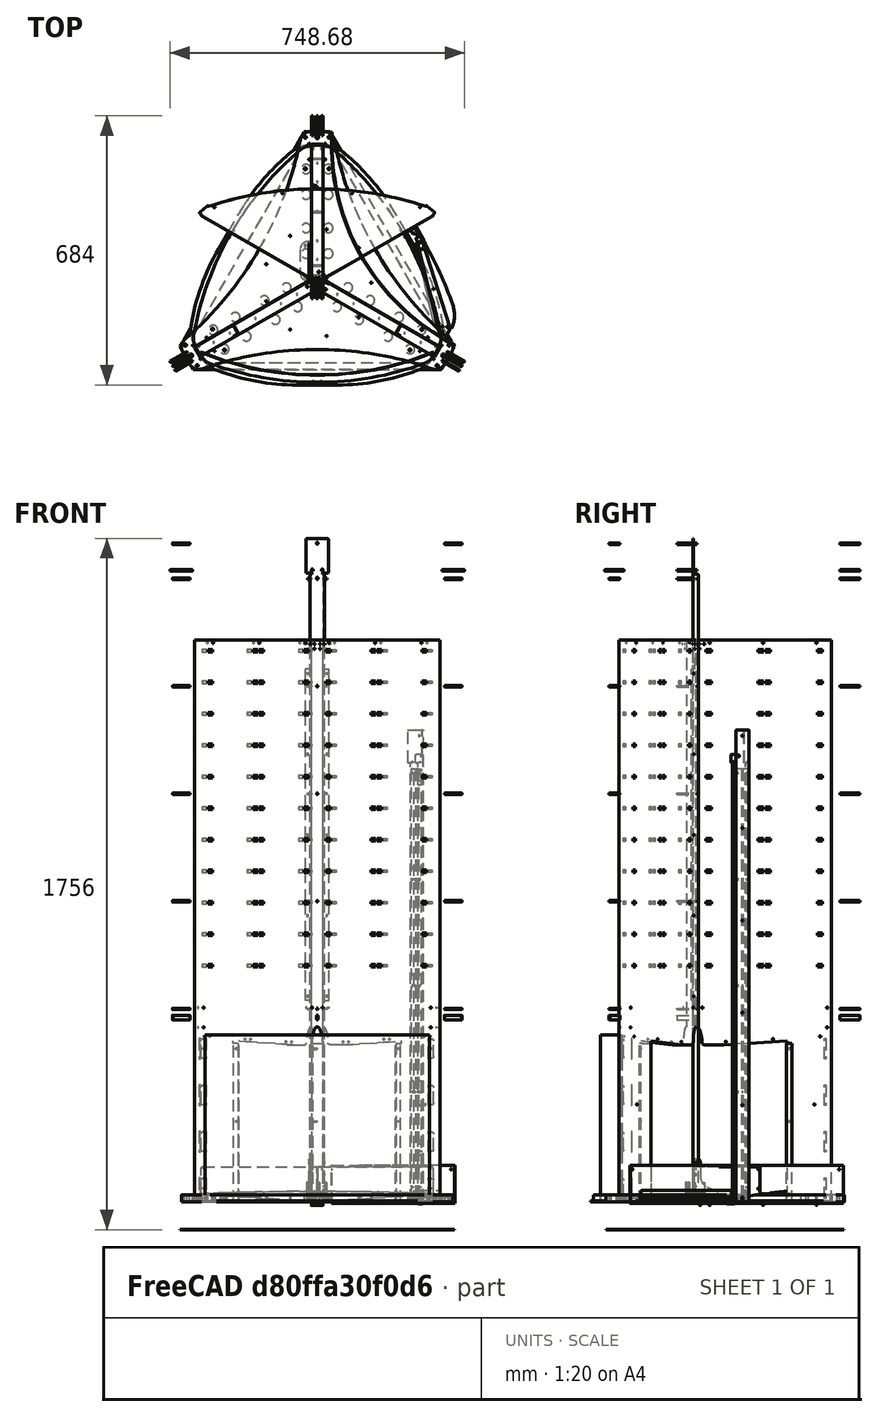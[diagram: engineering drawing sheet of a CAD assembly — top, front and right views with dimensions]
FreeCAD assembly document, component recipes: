
FREECAD ASSEMBLY — COMPONENT RECIPES ("composit_full_size3_door")

This assembly document has 79 components, labeled P0..P78 below (a component is one placed body or linked part). 75 of them carry a construction recipe — the FreeCAD feature program that regenerates the part from scratch, quoted from this document or its linked companion documents; the rest are supplied as boundary geometry only. No exploded tour is included for this assembly.
NOTE — document 3 of 3 of this assembly tour. The two overview renders and the header above are repeated from document 1; the component sections below continue where the previous document stopped.
COMPONENT P63 — recipe-attached ("sink_material_0.30ansi001", modeled in this document).
Construction recipe (the document's own serialized feature program — sketch geometry with constraints, then the solid features built on it; lengths are millimeters unless a unit is written):

FEATURE [Sketcher::SketchObject] Sketch037
  AttachmentSupport = -> [XY_Plane028]
  FullyConstrained = false
  MapMode = 5
  sketch-geometry (2):
    g0: LineSegment StartX=0 StartY=0 StartZ=0 EndX=74.4649 EndY=59.2839 EndZ=0
    g1: LineSegment StartX=0 StartY=0 StartZ=0 EndX=-93.8109 EndY=73.3435 EndZ=0
  constraints (2):
    c: Coincident(g0,g-1)
    c: Coincident(g1,g0)
FEATURE [Part::Part2DObjectPython] Line  label="sink_bend_line"  # Draft 2D object (typed FeaturePython)
  Area = 0
  AttachmentOffset = pos=(304.73,175.936,20) rot=(0,0,1;0rad)
  AttachmentSupport = -> [XY_Plane028]
  BendAngle = 6.48542
  ChamferSize = 0
  Closed = false
  End = (0,0,0)
  FaceAngle = 3.2479
  FilletRadius = 0
  Length = 352.44
  MakeFace = true
  MapMode = 5
  Placement = pos=(304.73,175.936,20) rot=(0,0,1;0rad)
  Points = (2) [(0,0,0),(-304.73,-175.936,-20)]
  Start = (304.73,175.936,20)
  Subdivisions = 0
  expr: .AttachmentOffset.Base.x = Spreadsheet.total_length * cos(30)
  expr: .AttachmentOffset.Base.y = Spreadsheet.total_length * sin(30)
  expr: BendAngle = atan2(.AttachmentOffset.Base.z; .AttachmentOffset.Base.y)
  expr: End = tuple(0; 0; 0)
  expr: FaceAngle = atan2(.AttachmentOffset.Base.z; Length)
FEATURE [PartDesign::Line] DatumLine
  AttacherType = Attacher::AttachEngineLine
  AttachmentSupport = -> [Z_Axis028]
  Length = 20
  MapMode = 29
  ResizeMode = 0
FEATURE [PartDesign::Line] DatumLine001
  AttacherType = Attacher::AttachEngineLine
  AttachmentSupport = -> [Line,X_Axis028]
  Length = 20
  MapMode = 24
  Placement = pos=(304.73,175.936,20) rot=(0.57735,-0.57735,-0.57735;2.0944rad)
  ResizeMode = 0
FEATURE [Sketcher::SketchObject] Sketch038
  AttachmentSupport = -> [Line]
  ExternalGeometry = -> [DatumLine001]
  FullyConstrained = false
  MapMode = 45
  Placement = pos=(152.365,87.9679,10) rot=(0.368581,0.6384,0.675717;2.39766rad)
  sketch-geometry (3):
    g0: LineSegment StartX=4.75e-14 StartY=4.27e-14 StartZ=0 EndX=4.75e-14 EndY=93.8582 EndZ=0
    g1: LineSegment StartX=4.75e-14 StartY=4.27e-14 StartZ=0 EndX=35.2298 EndY=3.46271 EndZ=0
    g2: ArcOfCircle CenterX=2.5 CenterY=2.75777 CenterZ=0 NormalX=0 NormalY=0 NormalZ=1 AngleXU=0 Radius=2.5 StartAngle=3.14159 EndAngle=4.81036
  constraints (9):
    c: Coincident(g0,g-1)
    c: Vertical(g0)
    c: Coincident(g1,g0)
    c: PointOnObject(g1,g-3)
    c: Angle(g-3) = 0.0979746
    c: Angle(g1,g0) = 1.47282  'bend_angle'
    c: Tangent(g2,g0) = 1.5708
    c: Tangent(g2,g1) = -1.5708
    c: Radius(g2) = 2.5
FEATURE [PartDesign::CoordinateSystem] Local_CS
  AttacherType = Attacher::AttachEngine3D
  AttachmentOffset = pos=(0,0,0) rot=(1,0,0;0.113192rad)
  AttachmentSupport = -> [XY_Plane028]
  MapMode = 5
  Placement = pos=(0,0,0) rot=(1,0,0;0.113192rad)
  expr: .AttachmentOffset.Rotation.Angle = Line.BendAngle
FEATURE [Sketcher::SketchObject] Sketch039
  AttachmentSupport = -> [Local_CS]
  ExternalGeometry = -> [Line,Sketch038]
  FullyConstrained = true
  MapMode = 5
  Placement = pos=(0,0,0) rot=(1,0,0;0.113192rad)
  sketch-geometry (3):
    g0: LineSegment StartX=2e-16 StartY=3.18954 StartZ=0 EndX=-459.172 EndY=270 EndZ=0
    g1: LineSegment StartX=2e-16 StartY=3.18954 StartZ=0 EndX=459.172 EndY=270 EndZ=0
    g2: LineSegment StartX=459.172 StartY=270 StartZ=0 EndX=-459.172 EndY=270 EndZ=0
  constraints (8):
    c: Coincident(g2,g1)
    c: DistanceY(g1) = 270
    c: Coincident(g0,g2)
    c: Symmetric(g1,g0,g-2)
    c: Coincident(g1,g0)
    c: PointOnObject(g0,g-2)
    c: Parallel(g1,g-3)
    c: PointOnObject(g-4,g1)
FEATURE [PartDesign::FeaturePython] BaseBend011  # WARN: FeaturePython — macro-defined, semantics opaque (R4)
  BendSide = 0
  BendSketch = -> Sketch039
  MidPlane = false
  Reverse = false
  Suppressed = false
  length = 100
  radius = 2
  thickness = 0.5
FEATURE [PartDesign::FeaturePython] Bend004  # WARN: FeaturePython — macro-defined, semantics opaque (R4)
  AutoMiter = false
  BaseFeature = -> BaseBend011
  BendType = 0
  LengthList = [100]
  LengthSpec = 1
  ReliefFactor = 0.7
  Suppressed = false
  UseReliefFactor = false
  angle = 95.6135
  baseObject = -> BaseBend011 [Edge3,Edge8]
  bendAList = [95.6135]
  extend1 = 2
  extend2 = 0
  gap1 = 0
  gap2 = 0
  invert = true
  kfactor = 0.5
  length = 100
  maxExtendDist = 5
  minGap = 0.1
  minReliefGap = 1
  miterangle1 = 0
  miterangle2 = 0
  offset = 0
  radius = 2
  reliefType = 0
  reliefd = 1
  reliefw = 0.8
  sketchflip = false
  sketchinvert = false
  unfold = false
  expr: angle = 180 deg - Sketch038.Constraints.bend_angle
  expr: radius = BaseBend011.radius
FEATURE [Sketcher::SketchObject] Sketch040
  AttachmentSupport = -> [Local_CS]
  ExternalGeometry = -> [Line,Sketch038]
  FullyConstrained = true
  MapMode = 5
  Placement = pos=(0,0,0) rot=(1,0,0;0.113192rad)
  sketch-geometry (13):
    g0: ArcOfCircle CenterX=0 CenterY=-630 CenterZ=0 NormalX=0 NormalY=0 NormalZ=1 AngleXU=0 Radius=870 StartAngle=1.24863 EndAngle=1.89296
    g1: LineSegment StartX=0 StartY=0 StartZ=0 EndX=294.959 EndY=171.391 EndZ=0
    g2: LineSegment StartX=150.979 StartY=90.9189 StartZ=0 EndX=293.573 EndY=173.776 EndZ=0
    g3: LineSegment StartX=-294.959 StartY=171.391 StartZ=0 EndX=0 EndY=0 EndZ=0
    g4: LineSegment StartX=-294.959 StartY=171.391 StartZ=0 EndX=-464.661 EndY=270 EndZ=0
    g5: LineSegment StartX=-464.661 StartY=270 StartZ=0 EndX=464.661 EndY=270 EndZ=0
    g6: LineSegment StartX=464.661 StartY=270 StartZ=0 EndX=294.959 EndY=171.391 EndZ=0
    g7: LineSegment StartX=294.959 StartY=171.391 StartZ=0 EndX=294.075 EndY=172.911 EndZ=0
    g8: LineSegment StartX=294.075 StartY=172.911 StartZ=0 EndX=293.573 EndY=173.776 EndZ=0
    g9: LineSegment StartX=-294.959 StartY=171.391 StartZ=0 EndX=-294.959 EndY=171.391 EndZ=0
    g10: LineSegment StartX=293.573 StartY=173.776 StartZ=0 EndX=275.46 EndY=195.241 EndZ=0
    g11: LineSegment StartX=-293.573 StartY=173.776 StartZ=0 EndX=-275.46 EndY=195.241 EndZ=0
    g12: LineSegment StartX=-294.959 StartY=171.391 StartZ=0 EndX=-293.573 EndY=173.776 EndZ=0
  constraints (34):
    c: Coincident(g1,g-1)
    c: PointOnObject(g1,g-3)
    c: Coincident(g7,g1)
    c: Distance(g1) = 341.139
    c: Coincident(g2,g-4)
    c: Parallel(g2,g1)
    c: DistanceY(g0) = -630
    c: Radius(g0) = 870
    c: Coincident(g9,g3)
    c: Coincident(g3,g1)
    c: Symmetric(g9,g7,g-2)
    c: Coincident(g4,g5)
    c: Coincident(g5,g6)
    c: Parallel(g6,g2)
    c: Symmetric(g5,g4,g-2)
    c: DistanceY(g5) = 270
    c: Coincident(g2,g8)
    c: Coincident(g7,g8)
    c: Perpendicular(g1,g7)
    c: Perpendicular(g1,g8)
    c: Distance(g8) = 1
    c: Coincident(g10,g0)
    c: Coincident(g11,g0)
    c: PointOnObject(g0,g-2)
    c: Coincident(g10,g8)
    c: Coincident(g12,g9)
    c: Coincident(g4,g12)
    c: Coincident(g12,g11)
    c: Symmetric(g4,g6,g-2)
    c: Symmetric(g8,g11,g-2)
    c: Horizontal(g0,g0)
    c: Distance(g10) = 28.0862
    c: Angle(g10,g2) = 1.39626
    c: Coincident(g6,g7)
FEATURE [PartDesign::SubShapeBinder] Binder031
  BindCopyOnChange = 0
  BindMode = 0
  ClaimChildren = false
  Context = -> Part007 [Body020.Binder031.]
  Fuse = false
  MakeFace = true
  OffsetFill = false
  OffsetIntersection = false
  OffsetJoinType = 0
  OffsetOpenResult = false
  PartialLoad = false
  Relative = true
  _Version = 2
FEATURE [PartDesign::Pocket] Pocket022
  BaseFeature = -> Bend004
  Direction = (0,0.11295,-0.993601)
  Length = 2.5
  Length2 = 5
  Profile = -> Sketch040
  ReferenceAxis = -> Sketch040 [N_Axis]
  Refine = true
  Reversed = true
  Suppressed = false
  Type = 0
FEATURE [Sketcher::SketchObject] Sketch042
  AttachmentSupport = -> [XY_Plane028]
  FullyConstrained = true
  MapMode = 5
  sketch-geometry (7):
    g0: LineSegment StartX=-18.3205 StartY=-10 StartZ=0 EndX=-0.5 EndY=0.288675 EndZ=0
    g1: LineSegment StartX=18.3205 StartY=-10 StartZ=0 EndX=-18.3205 EndY=-10 EndZ=0
    g2: LineSegment StartX=1 StartY=1.5e-15 StartZ=0 EndX=-1e-16 EndY=0.57735 EndZ=0
    g3: LineSegment StartX=1.3e-15 StartY=-2.2e-15 StartZ=0 EndX=0.5 EndY=0.288675 EndZ=0
    g4: LineSegment StartX=0.5 StartY=0.288675 StartZ=0 EndX=18.3205 EndY=-10 EndZ=0
    g5: LineSegment StartX=-2.6e-15 StartY=1.1547 StartZ=0 EndX=0.5 EndY=0.288675 EndZ=0
    g6: LineSegment StartX=-0.5 StartY=0.288675 StartZ=0 EndX=-2.6e-15 EndY=1.1547 EndZ=0
  constraints (19):
    c: Coincident(g4,g1)
    c: Coincident(g1,g0)
    c: Symmetric(g4,g0,g-2)
    c: PointOnObject(g2,g-1)
    c: PointOnObject(g2,g-2)
    c: Angle(g2) = 2.61799
    c: Distance(g-1,g2) = 0.5
    c: Coincident(g3,g-1)
    c: PointOnObject(g3,g2)
    c: Angle(g3) = 0.523599
    c: PointOnObject(g2,g4)
    c: Perpendicular(g3,g5)
    c: Coincident(g4,g5)
    c: Coincident(g4,g3)
    c: PointOnObject(g5,g-2)
    c: Coincident(g6,g0)
    c: Coincident(g6,g5)
    c: Symmetric(g4,g0,g-2)
    c: DistanceY(g1) = -10
FEATURE [Sketcher::SketchObject] Sketch041
  AttachmentOffset = pos=(0,0,0) rot=(0,1,0;0.523599rad)
  AttachmentSupport = -> [XZ_Plane028]
  ExternalGeometry = -> [Sketch038,Sketch042,Sketch040]
  FullyConstrained = false
  MapMode = 5
  Placement = pos=(0,0,0) rot=(0.935113,0.250563,0.250563;1.63783rad)
  sketch-geometry (16):
    g0: LineSegment StartX=340.573 StartY=19.628 StartZ=0 EndX=340.432 EndY=22.112 EndZ=0
    g1: LineSegment StartX=175.779 StartY=12.7533 StartZ=0 EndX=340.432 EndY=22.112 EndZ=0
    g2: LineSegment StartX=0.57735 StartY=196.491 StartZ=0 EndX=638.392 EndY=196.491 EndZ=0
    g3: LineSegment StartX=638.392 StartY=196.491 StartZ=0 EndX=638.392 EndY=36.5557 EndZ=0
    g4: LineSegment StartX=638.392 StartY=36.5557 StartZ=0 EndX=340.573 EndY=19.628 EndZ=0
    g5: LineSegment StartX=340.432 StartY=22.112 StartZ=0 EndX=340.432 EndY=85 EndZ=0
    g6: LineSegment StartX=0.57735 StartY=85 StartZ=0 EndX=0.57735 EndY=196.491 EndZ=0
    g7: LineSegment StartX=335.432 StartY=90 StartZ=0 EndX=5.57735 EndY=90 EndZ=0
    g8: ArcOfCircle CenterX=5.57735 CenterY=85 CenterZ=0 NormalX=0 NormalY=0 NormalZ=1 AngleXU=0 Radius=5 StartAngle=1.5708 EndAngle=3.14159
    g9: ArcOfCircle CenterX=335.432 CenterY=85 CenterZ=0 NormalX=0 NormalY=0 NormalZ=1 AngleXU=0 Radius=5 StartAngle=2e-16 EndAngle=1.5708
    g10: GeomPoint X=340.432 Y=90 Z=0
    g11: LineSegment StartX=0.57735 StartY=0 StartZ=0 EndX=0.57735 EndY=27.6603 EndZ=0
    g12: ArcOfCircle CenterX=5 CenterY=27.6603 CenterZ=0 NormalX=0 NormalY=0 NormalZ=1 AngleXU=0 Radius=4.42265 StartAngle=3.14159 EndAngle=4.18879
    g13: ArcOfCircle CenterX=0.57735 CenterY=20 CenterZ=0 NormalX=0 NormalY=0 NormalZ=1 AngleXU=0 Radius=4.42265 StartAngle=-2.31e-14 EndAngle=1.0472
    g14: LineSegment StartX=5 StartY=20 StartZ=0 EndX=5 EndY=0 EndZ=0
    g15: LineSegment StartX=5 StartY=0 StartZ=0 EndX=0.57735 EndY=0 EndZ=0
  constraints (39):
    c: Coincident(g1,g-3)
    c: Coincident(g1,g0)
    c: Perpendicular(g-3,g1)
    c: Perpendicular(g1,g0)
    c: Coincident(g5,g0)
    c: Coincident(g6,g2)
    c: Horizontal(g2)
    c: Coincident(g2,g3)
    c: Vertical(g3)
    c: Coincident(g3,g4)
    c: Coincident(g4,g0)
    c: Parallel(g4,g1)
    c: Vertical(g5)
    c: Vertical(g6)
    c: Vertical(g6,g-4)
    c: Horizontal(g7)
    c: Tangent(g8,g7) = -1.5708
    c: Tangent(g8,g6) = 1.5708
    c: PointOnObject(g10,g5)
    c: PointOnObject(g10,g7)
    c: Tangent(g5,g9) = -1.5708
    c: Tangent(g7,g9) = -1.5708
    c: Equal(g9,g8)
    c: Coincident(g11,g-4)
    c: Vertical(g11)
    c: PointOnObject(g13,g11)
    c: PointOnObject(g14,g-1)
    c: Vertical(g14)
    c: Coincident(g15,g14)
    c: Coincident(g15,g11)
    c: Tangent(g13,g12) = 1.5708
    c: Tangent(g12,g11) = 1.5708
    c: Tangent(g14,g13) = 1.5708
    c: Equal(g13,g12)
    c: DistanceX(g14) = 5
    c: DistanceY(g13) = 20
    c: DistanceY(g7) = 90
    c: Radius(g9) = 5
    c: Coincident(g0,g-5)
FEATURE [Sketcher::SketchObject] Sketch043
  AttachmentSupport = -> [Local_CS]
  FullyConstrained = false
  MapMode = 5
  Placement = pos=(0,0,0) rot=(1,0,0;0.113192rad)
  expr: Constraints[12] = Sketch038.Constraints.bend_angle / 2
  sketch-geometry (7):
    g0: ArcOfCircle CenterX=-2.2e-14 CenterY=1.72e-14 CenterZ=0 NormalX=0 NormalY=0 NormalZ=1 AngleXU=0 Radius=19.4106 StartAngle=5.52221 EndAngle=10.1858
    g1: ArcOfCircle CenterX=17.4885 CenterY=-16.6545 CenterZ=0 NormalX=0 NormalY=0 NormalZ=1 AngleXU=0 Radius=4.73935 StartAngle=2.38062 EndAngle=3.72466
    g2: ArcOfCircle CenterX=-17.4885 CenterY=-16.6545 CenterZ=0 NormalX=0 NormalY=0 NormalZ=1 AngleXU=0 Radius=4.73935 StartAngle=5.70012 EndAngle=7.04416
    g3: LineSegment StartX=13.5322 StartY=-19.2639 StartZ=0 EndX=49.1398 EndY=-73.2508 EndZ=0
    g4: LineSegment StartX=-13.5322 StartY=-19.2639 StartZ=0 EndX=-49.1398 EndY=-73.2508 EndZ=0
    g5: LineSegment StartX=-49.1398 StartY=-73.2508 StartZ=0 EndX=49.1398 EndY=-73.2508 EndZ=0
    g6: LineSegment StartX=-86.3387 StartY=-141.994 StartZ=0 EndX=130.665 EndY=54.7259 EndZ=0
  constraints (13):
    c: Coincident(g0,g-1)
    c: Coincident(g5,g4)
    c: Coincident(g5,g3)
    c: Tangent(g3,g1) = -1.5708
    c: Tangent(g1,g0) = 1.5708
    c: Tangent(g2,g0) = 1.5708
    c: Tangent(g4,g2) = 1.5708
    c: Symmetric(g4,g3,g-2)
    c: Symmetric(g2,g1,g-2)
    c: DistanceX(g1) = 13.5322
    c: DistanceY(g1) = -19.2639
    c: Angle(g3) = -0.987729
    c: Angle(g6) = 0.736411
FEATURE [Sketcher::SketchObject] Sketch064
  AttachmentSupport = -> [Local_CS]
  FullyConstrained = true
  MapMode = 5
  Placement = pos=(0,0,0) rot=(1,0,0;0.113192rad)
  expr: Constraints[3] = <<Properties>>.rivet_d
  sketch-geometry (4):
    g0: Circle CenterX=-88.3 CenterY=228.865 CenterZ=0 NormalX=0 NormalY=0 NormalZ=1 AngleXU=0 Radius=1.7
    g1: Circle CenterX=88.3 CenterY=228.865 CenterZ=0 NormalX=0 NormalY=0 NormalZ=1 AngleXU=0 Radius=1.7
    g2: Circle CenterX=261.291 CenterY=193.3 CenterZ=0 NormalX=0 NormalY=0 NormalZ=1 AngleXU=0 Radius=1.7
    g3: Circle CenterX=-261.291 CenterY=193.3 CenterZ=0 NormalX=0 NormalY=0 NormalZ=1 AngleXU=0 Radius=1.7
  constraints (10):
    c: Equal(g2,g1)
    c: Equal(g2,g0)
    c: Equal(g2,g3)
    c: Diameter(g2) = 3.4
    c: DistanceX(g1) = 88.3
    c: DistanceY(g1) = 228.865
    c: DistanceX(g2) = 261.291
    c: DistanceY(g2) = 193.3
    c: Symmetric(g0,g1,g-2)
    c: Symmetric(g3,g2,g-2)
FEATURE [PartDesign::FeaturePython] Bend030  # WARN: FeaturePython — macro-defined, semantics opaque (R4)
  AutoMiter = true
  BaseFeature = -> Pocket022
  BendType = 0
  LengthList = [10]
  LengthSpec = 0
  ReliefFactor = 0.7
  Suppressed = false
  UseReliefFactor = false
  angle = 90
  baseObject = -> Pocket022 [Edge44,Edge42]
  bendAList = [90]
  extend1 = 0
  extend2 = 0
  gap1 = 0
  gap2 = 0
  invert = false
  kfactor = 0.5
  length = 10
  maxExtendDist = 5
  minGap = 0.1
  minReliefGap = 1
  miterangle1 = 0
  miterangle2 = 0
  offset = 0
  radius = 2
  reliefType = 0
  reliefd = 1
  reliefw = 0.8
  sketchflip = false
  sketchinvert = false
  unfold = true
  expr: radius = BaseBend011.radius
FEATURE [Sketcher::SketchObject] Sketch219
  AttachmentSupport = -> [Bend030]
  ExternalGeometry = -> [Bend030]
  FullyConstrained = true
  MapMode = 5
  Placement = pos=(0,-1.69e-14,1.483e-13) rot=(1,0,0;3.25479rad)
  sketch-geometry (6):
    g0: LineSegment StartX=297.803 StartY=-177.345 StartZ=0 EndX=303.917 EndY=-182.504 EndZ=0
    g1: LineSegment StartX=303.917 StartY=-182.504 StartZ=0 EndX=285.803 EndY=-203.969 EndZ=0
    g2: LineSegment StartX=285.803 StartY=-203.969 StartZ=0 EndX=276.608 EndY=-196.209 EndZ=0
    g3: LineSegment StartX=279.192 StartY=-196.205 StartZ=0 EndX=297.807 EndY=-180.398 EndZ=0
    g4: ArcOfCircle CenterX=296.513 CenterY=-178.873 CenterZ=0 NormalX=0 NormalY=0 NormalZ=1 AngleXU=0 Radius=2 StartAngle=5.41641 EndAngle=7.15307
    g5: ArcOfCircle CenterX=277.898 CenterY=-194.681 CenterZ=0 NormalX=0 NormalY=0 NormalZ=1 AngleXU=0 Radius=2 StartAngle=4.01147 EndAngle=5.41641
  constraints (15):
    c: Coincident(g0,g-3)
    c: Coincident(g0,g1)
    c: Coincident(g1,g-3)
    c: Coincident(g1,g2)
    c: Perpendicular(g1,g2)
    c: Perpendicular(g0,g1)
    c: Tangent(g4,g0) = 1.5708
    c: Tangent(g5,g2) = 1.5708
    c: Tangent(g5,g3) = -1.5708
    c: Tangent(g4,g3) = -1.5708
    c: Equal(g4,g5)
    c: Radius(g4) = 2
    c: Distance(g0) = 8
    c: Distance(g2) = 12.0319
    c: Distance(g3,g1) = 10.0593
FEATURE [PartDesign::Pocket] Pocket131
  BaseFeature = -> Bend030
  Direction = (0,-0.11295,0.993601)
  Length = 5
  Length2 = 5
  Profile = -> Sketch219
  ReferenceAxis = -> Sketch219 [N_Axis]
  Suppressed = false
  Type = 0
FEATURE [PartDesign::Mirrored] Mirrored017
  BaseFeature = -> Pocket131
  MirrorPlane = -> YZ_Plane028
  Originals = -> [Pocket131]
  Suppressed = false
FEATURE [PartDesign::Pocket] Pocket024
  BaseFeature = -> Mirrored017
  Direction = (0,0,-1)
  Length = 5
  Length2 = 5
  Midplane = true
  Profile = -> Sketch042
  ReferenceAxis = -> Sketch042 [N_Axis]
  Suppressed = false
  Type = 1
FEATURE [PartDesign::FeaturePython] CornerRelief  # WARN: FeaturePython — macro-defined, semantics opaque (R4)
  BaseFeature = -> Pocket024
  ReliefSketch = 0
  Size = 6
  SizeRatio = 1.5
  Sketch = -> Sketch043
  Suppressed = false
  XOffset = 0
  YOffset = 0
  baseObject = -> Pocket024 [Edge28,Edge31]
  kfactor = 0.5
FEATURE [PartDesign::Pocket] Pocket023
  BaseFeature = -> CornerRelief
  Direction = (-0.5,0.866025,-1e-16)
  Length = 0.6
  Length2 = 5
  Profile = -> Sketch041
  ReferenceAxis = -> Sketch041 [N_Axis]
  Suppressed = false
  Type = 0
FEATURE [PartDesign::Mirrored] Mirrored002
  BaseFeature = -> Pocket023
  MirrorPlane = -> YZ_Plane028
  Originals = -> [Pocket023]
  Refine = true
  Suppressed = false
FEATURE [PartDesign::Boolean] Boolean008
  BaseFeature = -> Mirrored002
  Group = -> [Compound028]
  Suppressed = false
  Type = 1
  UsePlacement = false
  expr: Group = <<sink_fix001>>._self
FEATURE [PartDesign::Pocket] Pocket029
  BaseFeature = -> Boolean008
  Direction = (0,0.11295,-0.993601)
  Length = 5
  Length2 = 5
  Profile = -> Sketch064
  ReferenceAxis = -> Sketch064 [N_Axis]
  Reversed = true
  Suppressed = false
  Type = 1
FEATURE [PartDesign::Body] Body020  label="sink_material_0.30ansi"
  Group = -> [Sketch037,Line,DatumLine,Sketch038,DatumLine001,Sketch039,BaseBend011,Bend004,Local_CS,Sketch040,Binder031,Pocket022,Sketch041,Sketch042,Bend030,Sketch219,Pocket131,Mirrored017,Pocket024,Sketch043,CornerRelief,Pocket023,Mirrored002,Boolean008,Sketch064,Pocket029]
  Origin = -> Origin028
  Tip = -> Pocket029
COMPONENT P64 — recipe-attached ("Body110", modeled in this document).
Construction recipe (the document's own serialized feature program — sketch geometry with constraints, then the solid features built on it; lengths are millimeters unless a unit is written):

FEATURE [PartDesign::SubShapeBinder] Binder061
  BindCopyOnChange = 0
  BindMode = 0
  ClaimChildren = false
  Context = -> Part007 [Body021.Binder061.]
  Fuse = false
  MakeFace = true
  OffsetFill = false
  OffsetIntersection = false
  OffsetJoinType = 0
  OffsetOpenResult = false
  PartialLoad = false
  Relative = false
  Support = -> [Body020[Pocket022.Sketch040.]]
  _Version = 2
FEATURE [PartDesign::SubShapeBinder] Binder062
  BindCopyOnChange = 0
  BindMode = 0
  ClaimChildren = false
  Context = -> Part007 [Body021.Binder062.]
  Fuse = false
  MakeFace = true
  OffsetFill = false
  OffsetIntersection = false
  OffsetJoinType = 0
  OffsetOpenResult = false
  PartialLoad = false
  Relative = false
  Support = -> [Body020[Pocket029.Sketch064.]]
  _Version = 2
FEATURE [Sketcher::SketchObject] Sketch109
  AttachmentSupport = -> [XY_Plane029]
  ExternalGeometry = -> [Binder061]
  FullyConstrained = false
  MapMode = 5
  sketch-geometry (19):
    g0: ArcOfCircle CenterX=291.996 CenterY=172.865 CenterZ=0 NormalX=0 NormalY=0 NormalZ=1 AngleXU=0 Radius=1 StartAngle=5.23599 EndAngle=6.98132
    g1: LineSegment StartX=5.51e-14 StartY=239 StartZ=0 EndX=5.51e-14 EndY=240 EndZ=0
    g2: LineSegment StartX=292.496 StartY=171.999 StartZ=0 EndX=287.719 EndY=169.241 EndZ=0
    g3: ArcOfCircle CenterX=287.219 CenterY=170.107 CenterZ=0 NormalX=0 NormalY=0 NormalZ=1 AngleXU=0 Radius=1 StartAngle=3.90153 EndAngle=5.23599
    g4: LineSegment StartX=5.51e-14 StartY=239 StartZ=0 EndX=5.51e-14 EndY=224 EndZ=0
    g5: ArcOfCircle CenterX=243.002 CenterY=128.086 CenterZ=0 NormalX=0 NormalY=0 NormalZ=1 AngleXU=0 Radius=60 StartAngle=0.759936 EndAngle=1.27733
    g6: GeomPoint X=287.033 Y=168.845 Z=0
    g7: GeomPoint X=293.528 Y=172.595 Z=0
    g8: ArcOfCircle CenterX=1.26657 CenterY=-621.999 CenterZ=0 NormalX=0 NormalY=0 NormalZ=1 AngleXU=0 Radius=862 StartAngle=1.25533 EndAngle=1.57227
    g9: LineSegment StartX=5.28e-14 StartY=220.8 StartZ=0 EndX=5.51e-14 EndY=240 EndZ=0
    g10: ArcOfCircle CenterX=0 CenterY=-641.2 CenterZ=0 NormalX=0 NormalY=0 NormalZ=1 AngleXU=0 Radius=862 StartAngle=1.25386 EndAngle=1.5708
    g11: LineSegment StartX=5.51e-14 StartY=240 StartZ=0 EndX=268.713 EndY=197.462 EndZ=0
    g12: LineSegment StartX=5.28e-14 StartY=220.8 StartZ=0 EndX=268.65 EndY=177.867 EndZ=0
    g13: ArcOfCircle CenterX=0 CenterY=-676.059 CenterZ=0 NormalX=0 NormalY=0 NormalZ=1 AngleXU=0 Radius=900.059 StartAngle=1.27733 EndAngle=1.5708
    g14: Circle CenterX=268.65 CenterY=177.867 CenterZ=0 NormalX=0 NormalY=0 NormalZ=1 AngleXU=0 Radius=4
    g15: LineSegment StartX=0 StartY=0 StartZ=0 EndX=301.632 EndY=174.148 EndZ=0
    g16: LineSegment StartX=0 StartY=0 StartZ=0 EndX=-15 EndY=25.9808 EndZ=0
    g17: ArcOfCircle CenterX=262.507 CenterY=178.449 CenterZ=0 NormalX=0 NormalY=0 NormalZ=1 AngleXU=0 Radius=20 StartAngle=0.698132 EndAngle=1.25533
    g18: LineSegment StartX=292.762 StartY=173.508 StartZ=0 EndX=277.828 EndY=191.305 EndZ=0
  constraints (51):
    c: Tangent(g17,g8) = -1.5708
    c: Vertical(g1)
    c: PointOnObject(g1,g-2)
    c: Angle(g2) = -2.61799
    c: Tangent(g2,g0) = 1.5708
    c: DistanceY(g1,g1) = 1
    c: Tangent(g3,g2) = 1.5708
    c: Radius(g3) = 1
    c: Equal(g3,g0)
    c: Coincident(g4,g1)
    c: Vertical(g4)
    c: Distance(g4) = 15
    c: Tangent(g5,g3) = 1.5708
    c: PointOnObject(g7,g2)
    c: PointOnObject(g6,g2)
    c: PointOnObject(g6,g5)
    c: Coincident(g8,g1)
    c: PointOnObject(g9,g-2)
    c: DistanceY(g9,g4) = 3.2
    c: Coincident(g9,g1)
    c: Radius(g8) = 862  'outer_r'
    c: Distance(g6,g7) = 7.5
    c: PointOnObject(g10,g-2)
    c: Coincident(g11,g1)
    c: Coincident(g11,g17)
    c: Coincident(g12,g10)
    c: Coincident(g12,g10)
    c: Equal(g10,g8)
    c: Equal(g12,g11)
    c: Coincident(g10,g9)
    c: PointOnObject(g13,g-2)
    c: Coincident(g13,g4)
    c: Tangent(g13,g5) = -1.5708
    c: Coincident(g14,g10)
    c: Tangent(g14,g5)
    c: Radius(g14) = 4
    c: Coincident(g15,g-1)
    c: Angle(g15) = 0.523599
    c: Distance(g6,g15) = 2.7076
    c: DistanceY(g1) = 240
    c: Coincident(g16,g15)
    c: Perpendicular(g15,g16)
    c: Distance(g7,g16) = 340.5
    c: Tangent(g18,g0) = -1.5708
    c: Angle(g18) = 2.26893
    c: Tangent(g17,g18) = -1.5708
    c: PointOnObject(g8,g-5)
    c: Radius(g17) = 20
    c: PointOnObject(g7,g18)
    c: Radius(g5) = 60
    c: Distance(g16) = 30
FEATURE [PartDesign::Pad] Pad014
  Direction = (0,0,1)
  Length = 3
  Length2 = 10
  Profile = -> Sketch109
  ReferenceAxis = -> Sketch109 [N_Axis]
  Suppressed = false
  Type = 0
FEATURE [PartDesign::Mirrored] Mirrored008
  BaseFeature = -> Pad014
  MirrorPlane = -> Sketch109 [V_Axis]
  Originals = -> [Pad014]
  Refine = true
  Suppressed = false
FEATURE [PartDesign::Pocket] Pocket055
  BaseFeature = -> Mirrored008
  Direction = (0,0,-1)
  Length = 5
  Length2 = 5
  Profile = -> Binder062
  Reversed = true
  Suppressed = false
  Type = 0
FEATURE [PartDesign::Body] Body021
  Group = -> [Binder061,Binder062,Sketch109,Pad014,Mirrored008,Pocket055]
  Origin = -> Origin029
  Placement = pos=(0,0,0) rot=(1,0,0;0.116239rad)
  Tip = -> Pocket055
COMPONENT P65 — recipe-attached ("hat003", modeled in this document).
Construction recipe (the document's own serialized feature program — sketch geometry with constraints, then the solid features built on it; lengths are millimeters unless a unit is written):

FEATURE [PartDesign::SubShapeBinder] Binder041
  BindCopyOnChange = 0
  BindMode = 0
  ClaimChildren = true
  Context = -> Body076 [Binder041.]
  Fuse = false
  MakeFace = true
  OffsetFill = false
  OffsetIntersection = false
  OffsetJoinType = 0
  OffsetOpenResult = false
  PartialLoad = false
  Relative = false
  Support = -> [Array006]
  _Version = 2
FEATURE [PartDesign::Pad] Pad010
  Direction = (0,0,1)
  Length = 3
  Length2 = 10
  Profile = -> Binder041
  Suppressed = false
  Type = 0
FEATURE [Sketcher::SketchObject] Sketch072
  AttachmentSupport = -> [XY_Plane039]
  FullyConstrained = true
  MapMode = 5
  sketch-geometry (3):
    g0: Circle CenterX=122.567 CenterY=-102.846 CenterZ=0 NormalX=0 NormalY=0 NormalZ=1 AngleXU=0 Radius=15
    g1: Circle CenterX=-122.567 CenterY=-102.846 CenterZ=0 NormalX=0 NormalY=0 NormalZ=1 AngleXU=0 Radius=15
    g2: LineSegment StartX=0 StartY=0 StartZ=0 EndX=122.567 EndY=-102.846 EndZ=0
  constraints (7):
    c: Coincident(g2,g-1)
    c: Coincident(g2,g0)
    c: Angle(g2) = -0.698132
    c: Symmetric(g1,g0,g-2)
    c: Equal(g0,g1)
    c: Distance(g2) = 160
    c: Diameter(g0) = 30
FEATURE [PartDesign::Pocket] Pocket033
  BaseFeature = -> Pad010
  Direction = (0,0,-1)
  Length = 5
  Length2 = 5
  Midplane = true
  Profile = -> Sketch072
  ReferenceAxis = -> Sketch072 [N_Axis]
  Suppressed = false
  Type = 1
FEATURE [PartDesign::Body] Body076  label="hat_top"
  Group = -> [Binder041,Pad010,Sketch072,Pocket033]
  Origin = -> Origin039
  Placement = pos=(0,0,87) rot=(0,0,1;0rad)
  Tip = -> Pocket033
COMPONENT P66 — recipe-attached ("hat004", modeled in this document).
Construction recipe (the document's own serialized feature program — sketch geometry with constraints, then the solid features built on it; lengths are millimeters unless a unit is written):

FEATURE [PartDesign::SubShapeBinder] Binder039
  BindCopyOnChange = 0
  BindMode = 0
  ClaimChildren = true
  Context = -> Body075 [Binder039.]
  Fuse = false
  MakeFace = true
  OffsetFill = false
  OffsetIntersection = false
  OffsetJoinType = 0
  OffsetOpenResult = false
  PartialLoad = false
  Relative = false
  Support = -> [Array005]
  _Version = 2
FEATURE [PartDesign::Pad] Pad009
  Direction = (0,0,1)
  Length = 3
  Length2 = 10
  Profile = -> Binder039
  Suppressed = false
  Type = 0
FEATURE [PartDesign::SubShapeBinder] Binder040
  BindCopyOnChange = 0
  BindMode = 0
  ClaimChildren = true
  Context = -> Part010 [Body075.Binder040.]
  Fuse = false
  MakeFace = true
  OffsetFill = false
  OffsetIntersection = false
  OffsetJoinType = 0
  OffsetOpenResult = false
  PartialLoad = false
  Placement = pos=(0,382,0) rot=(0,0,1;3.14159rad)
  Relative = false
  Support = -> [Sketch066]
  _Version = 2
  expr: Support = Sketch066._self
FEATURE [PartDesign::Pocket] Pocket032
  BaseFeature = -> Pad009
  Direction = (0,0,-1)
  Length = 5
  Length2 = 5
  Midplane = true
  Profile = -> Binder040
  Suppressed = false
  Type = 1
FEATURE [Sketcher::SketchObject] Sketch098
  AttachmentSupport = -> [XY_Plane038]
  FullyConstrained = true
  MapMode = 5
  sketch-geometry (1):
    g0: Circle CenterX=0 CenterY=0 CenterZ=0 NormalX=0 NormalY=0 NormalZ=1 AngleXU=0 Radius=3.25
  constraints (2):
    c: Coincident(g0,g-1)
    c: Diameter(g0) = 6.5
FEATURE [PartDesign::SubShapeBinder] Binder054  label="socket_fixture"
  BindCopyOnChange = 0
  BindMode = 0
  ClaimChildren = false
  Context = -> Part010 [Body075.Binder054.]
  Fuse = false
  MakeFace = true
  OffsetFill = false
  OffsetIntersection = false
  OffsetJoinType = 0
  OffsetOpenResult = false
  PartialLoad = false
  Placement = pos=(69,65,0) rot=(0,0,1;3.14159rad)
  Relative = false
  Support = -> [<external socket_fixture.FCStd>#Sketch003]
  _Version = 2
  expr: Support = socket_fixture#<<fix_holes>>._self
FEATURE [PartDesign::SubShapeBinder] Binder055  label="driver_fixture"
  BindCopyOnChange = 0
  BindMode = 0
  ClaimChildren = false
  Context = -> Part010 [Body075.Binder055.]
  Fuse = false
  MakeFace = true
  OffsetFill = false
  OffsetIntersection = false
  OffsetJoinType = 0
  OffsetOpenResult = false
  PartialLoad = false
  Placement = pos=(-24,152,0) rot=(0,0,1;0rad)
  Relative = false
  Support = -> [<external UET-VAS-060A20_12V_IP20.FCStd>#Sketch001]
  _Version = 2
  expr: Support = <<UET-VAS-060A20_12V_IP20>>#<<holes>>._self
FEATURE [Sketcher::SketchObject] Sketch108
  AttachmentSupport = -> [XY_Plane038]
  ExternalGeometry = -> [Binder039]
  FullyConstrained = true
  MapMode = 5
  expr: Constraints[3] = <<Properties>>.rivet_d
  sketch-geometry (2):
    g0: LineSegment StartX=112.627 StartY=65.0251 StartZ=0 EndX=101.801 EndY=58.7751 EndZ=0
    g1: Circle CenterX=101.801 CenterY=58.7751 CenterZ=0 NormalX=0 NormalY=0 NormalZ=1 AngleXU=0 Radius=1.7
  constraints (5):
    c: Coincident(g0,g-3)
    c: PointOnObject(g-1,g0)
    c: Coincident(g1,g0)
    c: Diameter(g1) = 3.4
    c: Distance(g0) = 12.5
FEATURE [PartDesign::Pocket] Pocket054
  BaseFeature = -> Pocket032
  Direction = (0,0,-1)
  Length = 5
  Length2 = 5
  Profile = -> Sketch108
  ReferenceAxis = -> Sketch108 [N_Axis]
  Reversed = true
  Suppressed = false
  Type = 0
FEATURE [PartDesign::PolarPattern] PolarPattern
  Angle = 360
  Axis = -> Z_Axis038
  BaseFeature = -> Pocket054
  Mode = 0
  Occurrences = 3
  Offset = 120
  Originals = -> [Pocket032,Pocket054]
  Suppressed = false
FEATURE [PartDesign::Hole] Hole015
  BaseFeature = -> PolarPattern
  CustomThreadClearance = 0
  Depth = 25
  DepthType = 0
  Diameter = 27.5
  DrillForDepth = false
  DrillPoint = 1
  DrillPointAngle = 118
  HoleCutCountersinkAngle = 90
  HoleCutCustomValues = false
  HoleCutDepth = 0
  HoleCutDiameter = 0
  HoleCutType = 0
  ModelThread = false
  Profile = -> Sketch098
  Reversed = true
  Suppressed = false
  Tapered = false
  TaperedAngle = 90
  ThreadClass = 0
  ThreadDepth = 23.5
  ThreadDepthType = 0
  ThreadDirection = 0
  ThreadFit = 0
  ThreadSize = 0
  ThreadType = 0
  Threaded = false
  UseCustomThreadClearance = false
  expr: Diameter = <<sleeve_inner_sketch>>.Constraints.outer_r * 2 + 1.5 mm
FEATURE [PartDesign::Hole] Hole016
  BaseFeature = -> Hole015
  CustomThreadClearance = 0
  Depth = 25
  DepthType = 0
  Diameter = 3.4
  DrillForDepth = false
  DrillPoint = 1
  DrillPointAngle = 118
  HoleCutCountersinkAngle = 90
  HoleCutCustomValues = false
  HoleCutDepth = 0
  HoleCutDiameter = 0
  HoleCutType = 0
  ModelThread = false
  Profile = -> Binder054
  Reversed = true
  Suppressed = false
  Tapered = false
  TaperedAngle = 90
  ThreadClass = 0
  ThreadDepth = 23.5
  ThreadDepthType = 0
  ThreadDirection = 0
  ThreadFit = 0
  ThreadSize = 0
  ThreadType = 0
  Threaded = false
  UseCustomThreadClearance = false
  expr: Diameter = <<Properties>>.rivet_d
FEATURE [PartDesign::Hole] Hole017
  BaseFeature = -> Hole016
  CustomThreadClearance = 0
  Depth = 25
  DepthType = 0
  Diameter = 3.4
  DrillForDepth = false
  DrillPoint = 1
  DrillPointAngle = 118
  HoleCutCountersinkAngle = 90
  HoleCutCustomValues = false
  HoleCutDepth = 0
  HoleCutDiameter = 0
  HoleCutType = 0
  ModelThread = false
  Profile = -> Binder055
  Reversed = true
  Suppressed = false
  Tapered = false
  TaperedAngle = 90
  ThreadClass = 0
  ThreadDepth = 23.5
  ThreadDepthType = 0
  ThreadDirection = 0
  ThreadFit = 0
  ThreadSize = 0
  ThreadType = 0
  Threaded = false
  UseCustomThreadClearance = false
FEATURE [PartDesign::Mirrored] Mirrored006
  BaseFeature = -> Hole017
  MirrorPlane = -> YZ_Plane038
  Originals = -> [Hole016]
  Refine = true
  Suppressed = false
FEATURE [PartDesign::SubShapeBinder] Binder135
  BindCopyOnChange = 0
  BindMode = 0
  ClaimChildren = false
  Context = -> Part010 [Body075.Binder135.]
  Fuse = false
  MakeFace = true
  OffsetFill = false
  OffsetIntersection = false
  OffsetJoinType = 0
  OffsetOpenResult = false
  PartialLoad = false
  Placement = pos=(35,150,0) rot=(0,0,1;0rad)
  Relative = false
  Support = -> [Sketch226]
  _Version = 2
  expr: Support = <<UV_driver_holder_holes_Sketch>>._self
FEATURE [PartDesign::Hole] Hole
  BaseFeature = -> Mirrored006
  CustomThreadClearance = 0
  Depth = 25
  DepthType = 0
  Diameter = 3.4
  DrillForDepth = false
  DrillPoint = 1
  DrillPointAngle = 118
  HoleCutCountersinkAngle = 90
  HoleCutCustomValues = false
  HoleCutDepth = 0
  HoleCutDiameter = 6.1
  HoleCutType = 0
  ModelThread = false
  Profile = -> Binder135
  Reversed = true
  Suppressed = false
  Tapered = false
  TaperedAngle = 90
  ThreadClass = 0
  ThreadDepth = 25
  ThreadDepthType = 0
  ThreadDirection = 0
  ThreadFit = 0
  ThreadSize = 0
  ThreadType = 0
  Threaded = false
  UseCustomThreadClearance = false
  expr: Diameter = <<Properties>>.rivet_d
FEATURE [PartDesign::Boolean] Boolean035
  BaseFeature = -> Hole
  Group = -> [Compound084]
  Suppressed = false
  Type = 1
  UsePlacement = false
FEATURE [PartDesign::Body] Body075  label="hat_bottom_material_0.30ansi"
  Group = -> [Binder039,Pad009,Binder040,Pocket032,Pocket054,PolarPattern,Sketch098,Hole015,Binder054,Binder055,Hole016,Hole017,Mirrored006,Sketch108,Binder135,Hole,Boolean035]
  Origin = -> Origin038
  Tip = -> Boolean035
COMPONENT P67 — recipe-attached ("hat_plexiglass_material_0.30ansi001", modeled in this document).
Construction recipe (the document's own serialized feature program — sketch geometry with constraints, then the solid features built on it; lengths are millimeters unless a unit is written):

FEATURE [PartDesign::SubShapeBinder] Binder048
  BindCopyOnChange = 0
  BindMode = 0
  ClaimChildren = true
  Context = -> Part010 [Body078.Binder048.]
  Fuse = false
  MakeFace = true
  OffsetFill = false
  OffsetIntersection = false
  OffsetJoinType = 0
  OffsetOpenResult = false
  PartialLoad = false
  Relative = false
  Support = -> [Compound043]
  _Version = 2
FEATURE [PartDesign::FeaturePython] BaseBend022  # WARN: FeaturePython — macro-defined, semantics opaque (R4)
  BendSide = 1
  BendSketch = -> Binder048
  MidPlane = false
  Reverse = false
  Suppressed = false
  length = 96
  radius = 1
  thickness = 1.5
FEATURE [PartDesign::SubShapeBinder] Binder049
  BindCopyOnChange = 0
  BindMode = 0
  ClaimChildren = true
  Context = -> Part010 [Body078.Binder049.]
  Fuse = false
  MakeFace = false
  OffsetFill = false
  OffsetIntersection = false
  OffsetJoinType = 0
  OffsetOpenResult = false
  PartialLoad = false
  Placement = pos=(0,362,6) rot=(0.57735,0.57735,0.57735;2.0944rad)
  Relative = false
  Support = -> [Sketch073]
  _Version = 2
  expr: Support = Sketch073._self
FEATURE [PartDesign::Plane] DatumPlane003
  AttachmentOffset = pos=(0,0,0) rot=(0,1,0;0.523599rad)
  AttachmentSupport = -> [XZ_Plane043]
  Length = 648.977
  MapMode = 5
  Placement = pos=(0,0,0) rot=(0.935113,0.250563,0.250563;1.63783rad)
  ResizeMode = 0
  Width = 174.677
FEATURE [PartDesign::Hole] Hole010
  BaseFeature = -> BaseBend022
  CustomThreadClearance = 0
  Depth = 1303.68
  DepthType = 1
  Diameter = 3.4
  DrillForDepth = false
  DrillPoint = 1
  DrillPointAngle = 118
  HoleCutCountersinkAngle = 90
  HoleCutCustomValues = false
  HoleCutDepth = 0
  HoleCutDiameter = 6.1
  HoleCutType = 0
  ModelThread = false
  Profile = -> Binder049
  Reversed = true
  Suppressed = false
  Tapered = false
  TaperedAngle = 90
  ThreadClass = 0
  ThreadDepth = 1303.68
  ThreadDepthType = 0
  ThreadDirection = 0
  ThreadFit = 0
  ThreadSize = 0
  ThreadType = 0
  Threaded = false
  UseCustomThreadClearance = false
  expr: Diameter = <<Properties>>.rivet_d
FEATURE [Sketcher::SketchObject] Sketch081
  AttachmentOffset = pos=(0,0,0) rot=(0,1,0;-1.0472rad)
  AttachmentSupport = -> [XZ_Plane043]
  FullyConstrained = true
  MapMode = 5
  Placement = pos=(0,0,0) rot=(-0.774597,0.447214,0.447214;4.45971rad)
  expr: Constraints[2] = <<Properties>>.rivet_d
  sketch-geometry (1):
    g0: Circle CenterX=0 CenterY=19 CenterZ=0 NormalX=0 NormalY=0 NormalZ=1 AngleXU=0 Radius=1.7
  constraints (3):
    c: PointOnObject(g0,g-2)
    c: DistanceY(g0) = 19
    c: Diameter(g0) = 3.4
FEATURE [PartDesign::Mirrored] Mirrored005
  BaseFeature = -> Hole010
  MirrorPlane = -> DatumPlane003
  Originals = -> [Hole010]
  Refine = true
  Suppressed = false
FEATURE [PartDesign::SubShapeBinder] Binder050
  BindCopyOnChange = 0
  BindMode = 0
  ClaimChildren = true
  Context = -> Part010 [Body078.Binder050.]
  Fuse = false
  MakeFace = true
  OffsetFill = false
  OffsetIntersection = false
  OffsetJoinType = 0
  OffsetOpenResult = false
  PartialLoad = false
  Relative = false
  Support = -> [Body075[Binder039.Array005.Compound039.Sketch068.]]
  _Version = 2
FEATURE [Sketcher::SketchObject] Sketch082
  AttachmentSupport = -> [XY_Plane043]
  FullyConstrained = true
  MapMode = 5
FEATURE [PartDesign::Pocket] Pocket117
  BaseFeature = -> Mirrored005
  Direction = (0.866025,0.5,-1e-16)
  Length = 5
  Length2 = 5
  Midplane = true
  Profile = -> Sketch081
  ReferenceAxis = -> Sketch081 [N_Axis]
  Refine = true
  Suppressed = false
  Type = 1
FEATURE [PartDesign::Body] Body078  label="hat_plexiglass_material_0.30ansi"
  Group = -> [Binder048,BaseBend022,Binder049,DatumPlane003,Hole010,Sketch081,Mirrored005,Binder050,Sketch082,Pocket117]
  Origin = -> Origin043
  Placement = pos=(0,0,-3) rot=(0,0,1;0rad)
  Tip = -> Pocket117
COMPONENT P68 — recipe-attached ("top_amplifier_cornrer_material_0.50ansi001", modeled in this document).
Construction recipe (the document's own serialized feature program — sketch geometry with constraints, then the solid features built on it; lengths are millimeters unless a unit is written):

FEATURE [Sketcher::SketchObject] Sketch191  label="top_corner_base_sketch"
  AttachmentSupport = -> [XY_Plane087]
  FullyConstrained = true
  MapMode = 5
  sketch-geometry (2):
    g0: LineSegment StartX=-23.3827 StartY=13.5 StartZ=0 EndX=-5.116e-13 EndY=-3.109e-13 EndZ=0
    g1: LineSegment StartX=-5.131e-13 StartY=-3.108e-13 StartZ=0 EndX=23.3827 EndY=13.5 EndZ=0
  constraints (5):
    c: Coincident(g0,g-1)
    c: Coincident(g0,g1)
    c: Symmetric(g0,g1,g-2)
    c: Angle(g1,g0) = 2.0944
    c: Distance(g1) = 27  'length'
FEATURE [PartDesign::FeaturePython] BaseBend046  # WARN: FeaturePython — macro-defined, semantics opaque (R4)
  BendSide = 0
  BendSketch = -> Sketch191
  MidPlane = false
  Reverse = false
  Suppressed = false
  length = 30
  radius = 2
  thickness = 2
FEATURE [Sketcher::SketchObject] Sketch193
  AttachmentOffset = pos=(0,0,0) rot=(0,1,0;0.523599rad)
  AttachmentSupport = -> [XZ_Plane087]
  FullyConstrained = true
  MapMode = 5
  Placement = pos=(0,0,0) rot=(0.935113,0.250563,0.250563;1.63783rad)
  expr: Constraints[6] = <<top_corner_base_sketch>>.Constraints.length
  sketch-geometry (9):
    g0: LineSegment StartX=27 StartY=20 StartZ=0 EndX=27 EndY=0 EndZ=0
    g1: LineSegment StartX=27 StartY=0 StartZ=0 EndX=4 EndY=0 EndZ=0
    g2: ArcOfCircle CenterX=24 CenterY=21.3669 CenterZ=0 NormalX=0 NormalY=0 NormalZ=1 AngleXU=0 Radius=3 StartAngle=5.42813 EndAngle=6.28319
    g3: ArcOfCircle CenterX=2.87807 CenterY=3 CenterZ=0 NormalX=0 NormalY=0 NormalZ=1 AngleXU=0 Radius=3 StartAngle=4.71239 EndAngle=5.42813
    g4: LineSegment StartX=25.9685 StartY=19.1031 StartZ=0 EndX=27 EndY=20 EndZ=0
    g5: LineSegment StartX=4 StartY=0 StartZ=0 EndX=4.84661 EndY=0.736183 EndZ=0
    g6: LineSegment StartX=4.84661 StartY=0.736183 StartZ=0 EndX=25.9685 EndY=19.1031 EndZ=0
    g7: LineSegment StartX=2.87807 StartY=0 StartZ=0 EndX=4 EndY=0 EndZ=0
    g8: LineSegment StartX=27 StartY=20 StartZ=0 EndX=27 EndY=21.3669 EndZ=0
  constraints (24):
    c: PointOnObject(g5,g-1)
    c: Coincident(g4,g0)
    c: PointOnObject(g0,g-1)
    c: Vertical(g0)
    c: Coincident(g0,g1)
    c: Coincident(g1,g5)
    c: DistanceX(g0) = 27
    c: DistanceX(g5) = 4
    c: Tangent(g2,g0)
    c: Coincident(g5,g6)
    c: Coincident(g7,g1)
    c: Horizontal(g7)
    c: Coincident(g8,g0)
    c: Coincident(g8,g2)
    c: Vertical(g8)
    c: Equal(g3,g2)
    c: Radius(g3) = 3
    c: Tangent(g3,g6) = -1.5708
    c: Tangent(g6,g2) = -1.5708
    c: Coincident(g2,g4)
    c: Parallel(g4,g6)
    c: Parallel(g5,g6)
    c: Tangent(g7,g3) = -1.5708
    c: DistanceY(g0) = 20
FEATURE [PartDesign::FeaturePython] Bend029  # WARN: FeaturePython — macro-defined, semantics opaque (R4)
  AutoMiter = true
  BaseFeature = -> BaseBend046
  BendType = 0
  LengthList = [20]
  LengthSpec = 1
  ReliefFactor = 0.7
  Suppressed = false
  UseReliefFactor = false
  angle = 90
  baseObject = -> BaseBend046 [Edge17]
  bendAList = [90]
  extend1 = 0
  extend2 = 0
  gap1 = 0
  gap2 = 0
  invert = false
  kfactor = 0.5
  length = 20
  maxExtendDist = 5
  minGap = 0.1
  minReliefGap = 1
  miterangle1 = 0
  miterangle2 = 0
  offset = 0
  radius = 2
  reliefType = 0
  reliefd = 1
  reliefw = 0.8
  sketchflip = false
  sketchinvert = false
  unfold = false
  expr: radius = BaseBend046.radius
FEATURE [PartDesign::Fillet] Fillet014
  Base = -> Bend029 [Edge39,Edge2,Edge8]
  BaseFeature = -> Bend029
  Radius = 2
  SupportTransform = false
  Suppressed = false
  UseAllEdges = false
FEATURE [PartDesign::Pocket] Pocket118
  BaseFeature = -> Fillet014
  Direction = (-0.5,0.866025,-1e-16)
  Length = 5
  Length2 = 5
  Midplane = true
  Profile = -> Sketch193
  ReferenceAxis = -> Sketch193 [N_Axis]
  Suppressed = false
  Type = 1
FEATURE [PartDesign::Mirrored] Mirrored014
  BaseFeature = -> Pocket118
  MirrorPlane = -> YZ_Plane087
  Originals = -> [Pocket118]
  Suppressed = false
FEATURE [PartDesign::Boolean] Boolean017
  BaseFeature = -> Mirrored014
  Group = -> [Compound072]
  Refine = true
  Suppressed = false
  Type = 1
  UsePlacement = false
FEATURE [PartDesign::Body] Body113  label="top_amplifier_cornrer_material_0.50ansi"
  Group = -> [Sketch191,BaseBend046,Sketch193,Bend029,Fillet014,Pocket118,Mirrored014,Boolean017]
  Origin = -> Origin087
  Tip = -> Boolean017
COMPONENT P69 — recipe-attached ("sleeve_outer001", modeled in this document).
Construction recipe (the document's own serialized feature program — sketch geometry with constraints, then the solid features built on it; lengths are millimeters unless a unit is written):

FEATURE [Sketcher::SketchObject] Sketch220  label="sleeve_outer_sketch"
  AttachmentSupport = -> [XZ_Plane100]
  FullyConstrained = true
  MapMode = 5
  Placement = pos=(0,0,0) rot=(1,0,0;1.5708rad)
  expr: Constraints[13] = <<sleeve_inner_sketch>>.Constraints.outer_r + 0.25 mm
  sketch-geometry (6):
    g0: LineSegment StartX=13.25 StartY=67 StartZ=0 EndX=13.25 EndY=0 EndZ=0
    g1: LineSegment StartX=13.25 StartY=0 StartZ=0 EndX=35.25 EndY=0 EndZ=0
    g2: LineSegment StartX=35.25 StartY=0 StartZ=0 EndX=35.25 EndY=7 EndZ=0
    g3: LineSegment StartX=35.25 StartY=7 StartZ=0 EndX=20.25 EndY=7 EndZ=0
    g4: LineSegment StartX=20.25 StartY=7 StartZ=0 EndX=20.25 EndY=67 EndZ=0
    g5: LineSegment StartX=20.25 StartY=67 StartZ=0 EndX=13.25 EndY=67 EndZ=0
  constraints (20):
    c: PointOnObject(g0,g-1)
    c: Vertical(g0)
    c: Coincident(g0,g1)
    c: PointOnObject(g1,g-1)
    c: Coincident(g1,g2)
    c: Vertical(g2)
    c: Coincident(g2,g3)
    c: Horizontal(g3)
    c: Coincident(g3,g4)
    c: Vertical(g4)
    c: Coincident(g4,g5)
    c: Coincident(g5,g0)
    c: Horizontal(g5)
    c: DistanceX(g0) = 13.25
    c: DistanceX(g5,g5) = 7
    c: DistanceX(g3,g3) = 15
    c: DistanceY(g2,g2) = 7  'flange_height'
    c: DistanceY(g0,g0) = 67
    c: DistanceX(g3) = 20.25  'max_r'
    c: DistanceX(g1) = 35.25  'flange_max_r'
FEATURE [PartDesign::Revolution] Revolution001
  Angle = 360
  Angle2 = 60
  Axis = (0,2e-16,1)
  Base = (0,0,0)
  Placement = pos=(0,0,0) rot=(1,0,0;1.5708rad)
  Profile = -> Sketch220
  ReferenceAxis = -> Sketch220 [V_Axis]
  Reversed = true
  Suppressed = false
  Type = 0
FEATURE [PartDesign::Boolean] Boolean030
  BaseFeature = -> Revolution001
  Group = -> [Compound079]
  Suppressed = false
  Type = 1
  UsePlacement = false
FEATURE [PartDesign::CoordinateSystem] Local_CS039  label="sleeve_outer_flange_bottom_LCS"
  AttacherType = Attacher::AttachEngine3D
  AttachmentSupport = -> [XY_Plane100]
  MapMode = 5
FEATURE [PartDesign::CoordinateSystem] Local_CS040  label="sleeve_outer_end_LCS"
  AttacherType = Attacher::AttachEngine3D
  AttachmentOffset = pos=(0,0,67) rot=(0,0,1;0rad)
  AttachmentSupport = -> [XY_Plane100]
  MapMode = 5
  Placement = pos=(0,0,67) rot=(0,0,1;0rad)
FEATURE [PartDesign::Body] Body123  label="sleeve_outer"
  Group = -> [Sketch220,Revolution001,Boolean030,Local_CS039,Local_CS040]
  Origin = -> Origin100
  Tip = -> Boolean030
COMPONENT P70 — recipe-attached ("sleeve_inner001", modeled in this document).
Construction recipe (the document's own serialized feature program — sketch geometry with constraints, then the solid features built on it; lengths are millimeters unless a unit is written):

FEATURE [Sketcher::SketchObject] Sketch221  label="sleeve_inner_sketch"
  AttachmentSupport = -> [XZ_Plane101]
  FullyConstrained = true
  MapMode = 5
  Placement = pos=(0,0,0) rot=(1,0,0;1.5708rad)
  sketch-geometry (6):
    g0: LineSegment StartX=5 StartY=79 StartZ=0 EndX=5 EndY=0 EndZ=0
    g1: LineSegment StartX=5 StartY=0 StartZ=0 EndX=33 EndY=0 EndZ=0
    g2: LineSegment StartX=33 StartY=0 StartZ=0 EndX=33 EndY=8 EndZ=0
    g3: LineSegment StartX=33 StartY=8 StartZ=0 EndX=13 EndY=8 EndZ=0
    g4: LineSegment StartX=13 StartY=8 StartZ=0 EndX=13 EndY=79 EndZ=0
    g5: LineSegment StartX=13 StartY=79 StartZ=0 EndX=5 EndY=79 EndZ=0
  constraints (19):
    c: PointOnObject(g0,g-1)
    c: Vertical(g0)
    c: Coincident(g0,g1)
    c: PointOnObject(g1,g-1)
    c: Coincident(g1,g2)
    c: Vertical(g2)
    c: Coincident(g2,g3)
    c: Horizontal(g3)
    c: Coincident(g3,g4)
    c: Vertical(g4)
    c: Coincident(g4,g5)
    c: Coincident(g5,g0)
    c: Horizontal(g5)
    c: DistanceX(g0) = 5  'inner_r'
    c: DistanceX(g0,g3) = 8
    c: DistanceY(g2,g2) = 8
    c: DistanceX(g3,g3) = 20
    c: DistanceX(g3) = 13  'outer_r'
    c: DistanceY(g4,g4) = 71
FEATURE [PartDesign::Revolution] Revolution
  Angle = 360
  Angle2 = 60
  Axis = (0,2e-16,1)
  Base = (0,0,0)
  Placement = pos=(0,0,0) rot=(1,0,0;1.5708rad)
  Profile = -> Sketch221
  ReferenceAxis = -> Sketch221 [V_Axis]
  Reversed = true
  Suppressed = false
  Type = 0
FEATURE [PartDesign::Boolean] Boolean031
  BaseFeature = -> Revolution
  Group = -> [Compound083]
  Suppressed = false
  Type = 1
  UsePlacement = false
FEATURE [PartDesign::CoordinateSystem] Local_CS041  label="sleeve_inner_flange_top_LCS"
  AttacherType = Attacher::AttachEngine3D
  AttachmentOffset = pos=(0,0,8) rot=(0,0,1;0rad)
  AttachmentSupport = -> [XY_Plane101]
  MapMode = 5
  Placement = pos=(0,0,8) rot=(0,0,1;0rad)
FEATURE [PartDesign::CoordinateSystem] Local_CS042  label="sleeve_inner_end_LCS"
  AttacherType = Attacher::AttachEngine3D
  AttachmentOffset = pos=(0,0,79) rot=(0,0,1;0rad)
  AttachmentSupport = -> [XY_Plane101]
  MapMode = 5
  Placement = pos=(0,0,79) rot=(0,0,1;0rad)
FEATURE [PartDesign::Body] Body124  label="sleeve_inner"
  Group = -> [Sketch221,Revolution,Boolean031,Local_CS041,Local_CS042]
  Origin = -> Origin101
  Tip = -> Boolean031
COMPONENT P71 — geometry summary ("led_holder_fix_extrude001"; no construction recipe available for this part):
  bounding box: 1096.4 x 10.0 x 3.4 mm
  tessellated surface: 300 triangles
  volume: 454 mm^3 (1% of its bounding box)
  symmetry: 2-fold rotationally symmetric about the x axis; 2-fold rotationally symmetric about the y axis; revolution-symmetric about the z axis through its bounding-box center; mirror-symmetric across its x mid-plane, y mid-plane, z mid-plane
COMPONENT P72 — geometry summary ("pillar3_pillar3_dec_corner_common001"; no construction recipe available for this part):
  bounding box: 1187.4 x 57.6 x 25.7 mm
  tessellated surface: 1,508 triangles
  volume: 4069 mm^3 (0% of its bounding box)
  symmetry: mirror-symmetric across its x mid-plane
COMPONENT P73 — recipe-attached ("sink", modeled in this document).
Construction recipe (the document's own serialized feature program — sketch geometry with constraints, then the solid features built on it; lengths are millimeters unless a unit is written):

FEATURE [Sketcher::SketchObject] Sketch037
  AttachmentSupport = -> [XY_Plane028]
  FullyConstrained = false
  MapMode = 5
  sketch-geometry (2):
    g0: LineSegment StartX=0 StartY=0 StartZ=0 EndX=74.4649 EndY=59.2839 EndZ=0
    g1: LineSegment StartX=0 StartY=0 StartZ=0 EndX=-93.8109 EndY=73.3435 EndZ=0
  constraints (2):
    c: Coincident(g0,g-1)
    c: Coincident(g1,g0)
FEATURE [Part::Part2DObjectPython] Line  label="sink_bend_line"  # Draft 2D object (typed FeaturePython)
  Area = 0
  AttachmentOffset = pos=(304.73,175.936,20) rot=(0,0,1;0rad)
  AttachmentSupport = -> [XY_Plane028]
  BendAngle = 6.48542
  ChamferSize = 0
  Closed = false
  End = (0,0,0)
  FaceAngle = 3.2479
  FilletRadius = 0
  Length = 352.44
  MakeFace = true
  MapMode = 5
  Placement = pos=(304.73,175.936,20) rot=(0,0,1;0rad)
  Points = (2) [(0,0,0),(-304.73,-175.936,-20)]
  Start = (304.73,175.936,20)
  Subdivisions = 0
  expr: .AttachmentOffset.Base.x = Spreadsheet.total_length * cos(30)
  expr: .AttachmentOffset.Base.y = Spreadsheet.total_length * sin(30)
  expr: BendAngle = atan2(.AttachmentOffset.Base.z; .AttachmentOffset.Base.y)
  expr: End = tuple(0; 0; 0)
  expr: FaceAngle = atan2(.AttachmentOffset.Base.z; Length)
FEATURE [PartDesign::Line] DatumLine
  AttacherType = Attacher::AttachEngineLine
  AttachmentSupport = -> [Z_Axis028]
  Length = 20
  MapMode = 29
  ResizeMode = 0
FEATURE [PartDesign::Line] DatumLine001
  AttacherType = Attacher::AttachEngineLine
  AttachmentSupport = -> [Line,X_Axis028]
  Length = 20
  MapMode = 24
  Placement = pos=(304.73,175.936,20) rot=(0.57735,-0.57735,-0.57735;2.0944rad)
  ResizeMode = 0
FEATURE [Sketcher::SketchObject] Sketch038
  AttachmentSupport = -> [Line]
  ExternalGeometry = -> [DatumLine001]
  FullyConstrained = false
  MapMode = 45
  Placement = pos=(152.365,87.9679,10) rot=(0.368581,0.6384,0.675717;2.39766rad)
  sketch-geometry (3):
    g0: LineSegment StartX=4.75e-14 StartY=4.27e-14 StartZ=0 EndX=4.75e-14 EndY=93.8582 EndZ=0
    g1: LineSegment StartX=4.75e-14 StartY=4.27e-14 StartZ=0 EndX=35.2298 EndY=3.46271 EndZ=0
    g2: ArcOfCircle CenterX=2.5 CenterY=2.75777 CenterZ=0 NormalX=0 NormalY=0 NormalZ=1 AngleXU=0 Radius=2.5 StartAngle=3.14159 EndAngle=4.81036
  constraints (9):
    c: Coincident(g0,g-1)
    c: Vertical(g0)
    c: Coincident(g1,g0)
    c: PointOnObject(g1,g-3)
    c: Angle(g-3) = 0.0979746
    c: Angle(g1,g0) = 1.47282  'bend_angle'
    c: Tangent(g2,g0) = 1.5708
    c: Tangent(g2,g1) = -1.5708
    c: Radius(g2) = 2.5
FEATURE [PartDesign::CoordinateSystem] Local_CS
  AttacherType = Attacher::AttachEngine3D
  AttachmentOffset = pos=(0,0,0) rot=(1,0,0;0.113192rad)
  AttachmentSupport = -> [XY_Plane028]
  MapMode = 5
  Placement = pos=(0,0,0) rot=(1,0,0;0.113192rad)
  expr: .AttachmentOffset.Rotation.Angle = Line.BendAngle
FEATURE [Sketcher::SketchObject] Sketch039
  AttachmentSupport = -> [Local_CS]
  ExternalGeometry = -> [Line,Sketch038]
  FullyConstrained = true
  MapMode = 5
  Placement = pos=(0,0,0) rot=(1,0,0;0.113192rad)
  sketch-geometry (3):
    g0: LineSegment StartX=2e-16 StartY=3.18954 StartZ=0 EndX=-459.172 EndY=270 EndZ=0
    g1: LineSegment StartX=2e-16 StartY=3.18954 StartZ=0 EndX=459.172 EndY=270 EndZ=0
    g2: LineSegment StartX=459.172 StartY=270 StartZ=0 EndX=-459.172 EndY=270 EndZ=0
  constraints (8):
    c: Coincident(g2,g1)
    c: DistanceY(g1) = 270
    c: Coincident(g0,g2)
    c: Symmetric(g1,g0,g-2)
    c: Coincident(g1,g0)
    c: PointOnObject(g0,g-2)
    c: Parallel(g1,g-3)
    c: PointOnObject(g-4,g1)
FEATURE [PartDesign::FeaturePython] BaseBend011  # WARN: FeaturePython — macro-defined, semantics opaque (R4)
  BendSide = 0
  BendSketch = -> Sketch039
  MidPlane = false
  Reverse = false
  Suppressed = false
  length = 100
  radius = 2
  thickness = 0.5
FEATURE [PartDesign::FeaturePython] Bend004  # WARN: FeaturePython — macro-defined, semantics opaque (R4)
  AutoMiter = false
  BaseFeature = -> BaseBend011
  BendType = 0
  LengthList = [100]
  LengthSpec = 1
  ReliefFactor = 0.7
  Suppressed = false
  UseReliefFactor = false
  angle = 95.6135
  baseObject = -> BaseBend011 [Edge3,Edge8]
  bendAList = [95.6135]
  extend1 = 2
  extend2 = 0
  gap1 = 0
  gap2 = 0
  invert = true
  kfactor = 0.5
  length = 100
  maxExtendDist = 5
  minGap = 0.1
  minReliefGap = 1
  miterangle1 = 0
  miterangle2 = 0
  offset = 0
  radius = 2
  reliefType = 0
  reliefd = 1
  reliefw = 0.8
  sketchflip = false
  sketchinvert = false
  unfold = false
  expr: angle = 180 deg - Sketch038.Constraints.bend_angle
  expr: radius = BaseBend011.radius
FEATURE [Sketcher::SketchObject] Sketch040
  AttachmentSupport = -> [Local_CS]
  ExternalGeometry = -> [Line,Sketch038]
  FullyConstrained = true
  MapMode = 5
  Placement = pos=(0,0,0) rot=(1,0,0;0.113192rad)
  sketch-geometry (13):
    g0: ArcOfCircle CenterX=0 CenterY=-630 CenterZ=0 NormalX=0 NormalY=0 NormalZ=1 AngleXU=0 Radius=870 StartAngle=1.24863 EndAngle=1.89296
    g1: LineSegment StartX=0 StartY=0 StartZ=0 EndX=294.959 EndY=171.391 EndZ=0
    g2: LineSegment StartX=150.979 StartY=90.9189 StartZ=0 EndX=293.573 EndY=173.776 EndZ=0
    g3: LineSegment StartX=-294.959 StartY=171.391 StartZ=0 EndX=0 EndY=0 EndZ=0
    g4: LineSegment StartX=-294.959 StartY=171.391 StartZ=0 EndX=-464.661 EndY=270 EndZ=0
    g5: LineSegment StartX=-464.661 StartY=270 StartZ=0 EndX=464.661 EndY=270 EndZ=0
    g6: LineSegment StartX=464.661 StartY=270 StartZ=0 EndX=294.959 EndY=171.391 EndZ=0
    g7: LineSegment StartX=294.959 StartY=171.391 StartZ=0 EndX=294.075 EndY=172.911 EndZ=0
    g8: LineSegment StartX=294.075 StartY=172.911 StartZ=0 EndX=293.573 EndY=173.776 EndZ=0
    g9: LineSegment StartX=-294.959 StartY=171.391 StartZ=0 EndX=-294.959 EndY=171.391 EndZ=0
    g10: LineSegment StartX=293.573 StartY=173.776 StartZ=0 EndX=275.46 EndY=195.241 EndZ=0
    g11: LineSegment StartX=-293.573 StartY=173.776 StartZ=0 EndX=-275.46 EndY=195.241 EndZ=0
    g12: LineSegment StartX=-294.959 StartY=171.391 StartZ=0 EndX=-293.573 EndY=173.776 EndZ=0
  constraints (34):
    c: Coincident(g1,g-1)
    c: PointOnObject(g1,g-3)
    c: Coincident(g7,g1)
    c: Distance(g1) = 341.139
    c: Coincident(g2,g-4)
    c: Parallel(g2,g1)
    c: DistanceY(g0) = -630
    c: Radius(g0) = 870
    c: Coincident(g9,g3)
    c: Coincident(g3,g1)
    c: Symmetric(g9,g7,g-2)
    c: Coincident(g4,g5)
    c: Coincident(g5,g6)
    c: Parallel(g6,g2)
    c: Symmetric(g5,g4,g-2)
    c: DistanceY(g5) = 270
    c: Coincident(g2,g8)
    c: Coincident(g7,g8)
    c: Perpendicular(g1,g7)
    c: Perpendicular(g1,g8)
    c: Distance(g8) = 1
    c: Coincident(g10,g0)
    c: Coincident(g11,g0)
    c: PointOnObject(g0,g-2)
    c: Coincident(g10,g8)
    c: Coincident(g12,g9)
    c: Coincident(g4,g12)
    c: Coincident(g12,g11)
    c: Symmetric(g4,g6,g-2)
    c: Symmetric(g8,g11,g-2)
    c: Horizontal(g0,g0)
    c: Distance(g10) = 28.0862
    c: Angle(g10,g2) = 1.39626
    c: Coincident(g6,g7)
FEATURE [PartDesign::SubShapeBinder] Binder031
  BindCopyOnChange = 0
  BindMode = 0
  ClaimChildren = false
  Context = -> Part007 [Body020.Binder031.]
  Fuse = false
  MakeFace = true
  OffsetFill = false
  OffsetIntersection = false
  OffsetJoinType = 0
  OffsetOpenResult = false
  PartialLoad = false
  Relative = true
  _Version = 2
FEATURE [PartDesign::Pocket] Pocket022
  BaseFeature = -> Bend004
  Direction = (0,0.11295,-0.993601)
  Length = 2.5
  Length2 = 5
  Profile = -> Sketch040
  ReferenceAxis = -> Sketch040 [N_Axis]
  Refine = true
  Reversed = true
  Suppressed = false
  Type = 0
FEATURE [Sketcher::SketchObject] Sketch042
  AttachmentSupport = -> [XY_Plane028]
  FullyConstrained = true
  MapMode = 5
  sketch-geometry (7):
    g0: LineSegment StartX=-18.3205 StartY=-10 StartZ=0 EndX=-0.5 EndY=0.288675 EndZ=0
    g1: LineSegment StartX=18.3205 StartY=-10 StartZ=0 EndX=-18.3205 EndY=-10 EndZ=0
    g2: LineSegment StartX=1 StartY=1.5e-15 StartZ=0 EndX=-1e-16 EndY=0.57735 EndZ=0
    g3: LineSegment StartX=1.3e-15 StartY=-2.2e-15 StartZ=0 EndX=0.5 EndY=0.288675 EndZ=0
    g4: LineSegment StartX=0.5 StartY=0.288675 StartZ=0 EndX=18.3205 EndY=-10 EndZ=0
    g5: LineSegment StartX=-2.6e-15 StartY=1.1547 StartZ=0 EndX=0.5 EndY=0.288675 EndZ=0
    g6: LineSegment StartX=-0.5 StartY=0.288675 StartZ=0 EndX=-2.6e-15 EndY=1.1547 EndZ=0
  constraints (19):
    c: Coincident(g4,g1)
    c: Coincident(g1,g0)
    c: Symmetric(g4,g0,g-2)
    c: PointOnObject(g2,g-1)
    c: PointOnObject(g2,g-2)
    c: Angle(g2) = 2.61799
    c: Distance(g-1,g2) = 0.5
    c: Coincident(g3,g-1)
    c: PointOnObject(g3,g2)
    c: Angle(g3) = 0.523599
    c: PointOnObject(g2,g4)
    c: Perpendicular(g3,g5)
    c: Coincident(g4,g5)
    c: Coincident(g4,g3)
    c: PointOnObject(g5,g-2)
    c: Coincident(g6,g0)
    c: Coincident(g6,g5)
    c: Symmetric(g4,g0,g-2)
    c: DistanceY(g1) = -10
FEATURE [Sketcher::SketchObject] Sketch041
  AttachmentOffset = pos=(0,0,0) rot=(0,1,0;0.523599rad)
  AttachmentSupport = -> [XZ_Plane028]
  ExternalGeometry = -> [Sketch038,Sketch042,Sketch040]
  FullyConstrained = false
  MapMode = 5
  Placement = pos=(0,0,0) rot=(0.935113,0.250563,0.250563;1.63783rad)
  sketch-geometry (16):
    g0: LineSegment StartX=340.573 StartY=19.628 StartZ=0 EndX=340.432 EndY=22.112 EndZ=0
    g1: LineSegment StartX=175.779 StartY=12.7533 StartZ=0 EndX=340.432 EndY=22.112 EndZ=0
    g2: LineSegment StartX=0.57735 StartY=196.491 StartZ=0 EndX=638.392 EndY=196.491 EndZ=0
    g3: LineSegment StartX=638.392 StartY=196.491 StartZ=0 EndX=638.392 EndY=36.5557 EndZ=0
    g4: LineSegment StartX=638.392 StartY=36.5557 StartZ=0 EndX=340.573 EndY=19.628 EndZ=0
    g5: LineSegment StartX=340.432 StartY=22.112 StartZ=0 EndX=340.432 EndY=85 EndZ=0
    g6: LineSegment StartX=0.57735 StartY=85 StartZ=0 EndX=0.57735 EndY=196.491 EndZ=0
    g7: LineSegment StartX=335.432 StartY=90 StartZ=0 EndX=5.57735 EndY=90 EndZ=0
    g8: ArcOfCircle CenterX=5.57735 CenterY=85 CenterZ=0 NormalX=0 NormalY=0 NormalZ=1 AngleXU=0 Radius=5 StartAngle=1.5708 EndAngle=3.14159
    g9: ArcOfCircle CenterX=335.432 CenterY=85 CenterZ=0 NormalX=0 NormalY=0 NormalZ=1 AngleXU=0 Radius=5 StartAngle=2e-16 EndAngle=1.5708
    g10: GeomPoint X=340.432 Y=90 Z=0
    g11: LineSegment StartX=0.57735 StartY=0 StartZ=0 EndX=0.57735 EndY=27.6603 EndZ=0
    g12: ArcOfCircle CenterX=5 CenterY=27.6603 CenterZ=0 NormalX=0 NormalY=0 NormalZ=1 AngleXU=0 Radius=4.42265 StartAngle=3.14159 EndAngle=4.18879
    g13: ArcOfCircle CenterX=0.57735 CenterY=20 CenterZ=0 NormalX=0 NormalY=0 NormalZ=1 AngleXU=0 Radius=4.42265 StartAngle=-2.31e-14 EndAngle=1.0472
    g14: LineSegment StartX=5 StartY=20 StartZ=0 EndX=5 EndY=0 EndZ=0
    g15: LineSegment StartX=5 StartY=0 StartZ=0 EndX=0.57735 EndY=0 EndZ=0
  constraints (39):
    c: Coincident(g1,g-3)
    c: Coincident(g1,g0)
    c: Perpendicular(g-3,g1)
    c: Perpendicular(g1,g0)
    c: Coincident(g5,g0)
    c: Coincident(g6,g2)
    c: Horizontal(g2)
    c: Coincident(g2,g3)
    c: Vertical(g3)
    c: Coincident(g3,g4)
    c: Coincident(g4,g0)
    c: Parallel(g4,g1)
    c: Vertical(g5)
    c: Vertical(g6)
    c: Vertical(g6,g-4)
    c: Horizontal(g7)
    c: Tangent(g8,g7) = -1.5708
    c: Tangent(g8,g6) = 1.5708
    c: PointOnObject(g10,g5)
    c: PointOnObject(g10,g7)
    c: Tangent(g5,g9) = -1.5708
    c: Tangent(g7,g9) = -1.5708
    c: Equal(g9,g8)
    c: Coincident(g11,g-4)
    c: Vertical(g11)
    c: PointOnObject(g13,g11)
    c: PointOnObject(g14,g-1)
    c: Vertical(g14)
    c: Coincident(g15,g14)
    c: Coincident(g15,g11)
    c: Tangent(g13,g12) = 1.5708
    c: Tangent(g12,g11) = 1.5708
    c: Tangent(g14,g13) = 1.5708
    c: Equal(g13,g12)
    c: DistanceX(g14) = 5
    c: DistanceY(g13) = 20
    c: DistanceY(g7) = 90
    c: Radius(g9) = 5
    c: Coincident(g0,g-5)
FEATURE [Sketcher::SketchObject] Sketch043
  AttachmentSupport = -> [Local_CS]
  FullyConstrained = false
  MapMode = 5
  Placement = pos=(0,0,0) rot=(1,0,0;0.113192rad)
  expr: Constraints[12] = Sketch038.Constraints.bend_angle / 2
  sketch-geometry (7):
    g0: ArcOfCircle CenterX=-2.2e-14 CenterY=1.72e-14 CenterZ=0 NormalX=0 NormalY=0 NormalZ=1 AngleXU=0 Radius=19.4106 StartAngle=5.52221 EndAngle=10.1858
    g1: ArcOfCircle CenterX=17.4885 CenterY=-16.6545 CenterZ=0 NormalX=0 NormalY=0 NormalZ=1 AngleXU=0 Radius=4.73935 StartAngle=2.38062 EndAngle=3.72466
    g2: ArcOfCircle CenterX=-17.4885 CenterY=-16.6545 CenterZ=0 NormalX=0 NormalY=0 NormalZ=1 AngleXU=0 Radius=4.73935 StartAngle=5.70012 EndAngle=7.04416
    g3: LineSegment StartX=13.5322 StartY=-19.2639 StartZ=0 EndX=49.1398 EndY=-73.2508 EndZ=0
    g4: LineSegment StartX=-13.5322 StartY=-19.2639 StartZ=0 EndX=-49.1398 EndY=-73.2508 EndZ=0
    g5: LineSegment StartX=-49.1398 StartY=-73.2508 StartZ=0 EndX=49.1398 EndY=-73.2508 EndZ=0
    g6: LineSegment StartX=-86.3387 StartY=-141.994 StartZ=0 EndX=130.665 EndY=54.7259 EndZ=0
  constraints (13):
    c: Coincident(g0,g-1)
    c: Coincident(g5,g4)
    c: Coincident(g5,g3)
    c: Tangent(g3,g1) = -1.5708
    c: Tangent(g1,g0) = 1.5708
    c: Tangent(g2,g0) = 1.5708
    c: Tangent(g4,g2) = 1.5708
    c: Symmetric(g4,g3,g-2)
    c: Symmetric(g2,g1,g-2)
    c: DistanceX(g1) = 13.5322
    c: DistanceY(g1) = -19.2639
    c: Angle(g3) = -0.987729
    c: Angle(g6) = 0.736411
FEATURE [Sketcher::SketchObject] Sketch064
  AttachmentSupport = -> [Local_CS]
  FullyConstrained = true
  MapMode = 5
  Placement = pos=(0,0,0) rot=(1,0,0;0.113192rad)
  expr: Constraints[3] = <<Properties>>.rivet_d
  sketch-geometry (4):
    g0: Circle CenterX=-88.3 CenterY=228.865 CenterZ=0 NormalX=0 NormalY=0 NormalZ=1 AngleXU=0 Radius=1.7
    g1: Circle CenterX=88.3 CenterY=228.865 CenterZ=0 NormalX=0 NormalY=0 NormalZ=1 AngleXU=0 Radius=1.7
    g2: Circle CenterX=261.291 CenterY=193.3 CenterZ=0 NormalX=0 NormalY=0 NormalZ=1 AngleXU=0 Radius=1.7
    g3: Circle CenterX=-261.291 CenterY=193.3 CenterZ=0 NormalX=0 NormalY=0 NormalZ=1 AngleXU=0 Radius=1.7
  constraints (10):
    c: Equal(g2,g1)
    c: Equal(g2,g0)
    c: Equal(g2,g3)
    c: Diameter(g2) = 3.4
    c: DistanceX(g1) = 88.3
    c: DistanceY(g1) = 228.865
    c: DistanceX(g2) = 261.291
    c: DistanceY(g2) = 193.3
    c: Symmetric(g0,g1,g-2)
    c: Symmetric(g3,g2,g-2)
FEATURE [PartDesign::SubShapeBinder] Binder061
  BindCopyOnChange = 0
  BindMode = 0
  ClaimChildren = false
  Context = -> Part007 [Body021.Binder061.]
  Fuse = false
  MakeFace = true
  OffsetFill = false
  OffsetIntersection = false
  OffsetJoinType = 0
  OffsetOpenResult = false
  PartialLoad = false
  Relative = false
  Support = -> [Body020[Pocket022.Sketch040.]]
  _Version = 2
FEATURE [PartDesign::SubShapeBinder] Binder062
  BindCopyOnChange = 0
  BindMode = 0
  ClaimChildren = false
  Context = -> Part007 [Body021.Binder062.]
  Fuse = false
  MakeFace = true
  OffsetFill = false
  OffsetIntersection = false
  OffsetJoinType = 0
  OffsetOpenResult = false
  PartialLoad = false
  Relative = false
  Support = -> [Body020[Pocket029.Sketch064.]]
  _Version = 2
FEATURE [Sketcher::SketchObject] Sketch109
  AttachmentSupport = -> [XY_Plane029]
  ExternalGeometry = -> [Binder061]
  FullyConstrained = false
  MapMode = 5
  sketch-geometry (19):
    g0: ArcOfCircle CenterX=291.996 CenterY=172.865 CenterZ=0 NormalX=0 NormalY=0 NormalZ=1 AngleXU=0 Radius=1 StartAngle=5.23599 EndAngle=6.98132
    g1: LineSegment StartX=5.51e-14 StartY=239 StartZ=0 EndX=5.51e-14 EndY=240 EndZ=0
    g2: LineSegment StartX=292.496 StartY=171.999 StartZ=0 EndX=287.719 EndY=169.241 EndZ=0
    g3: ArcOfCircle CenterX=287.219 CenterY=170.107 CenterZ=0 NormalX=0 NormalY=0 NormalZ=1 AngleXU=0 Radius=1 StartAngle=3.90153 EndAngle=5.23599
    g4: LineSegment StartX=5.51e-14 StartY=239 StartZ=0 EndX=5.51e-14 EndY=224 EndZ=0
    g5: ArcOfCircle CenterX=243.002 CenterY=128.086 CenterZ=0 NormalX=0 NormalY=0 NormalZ=1 AngleXU=0 Radius=60 StartAngle=0.759936 EndAngle=1.27733
    g6: GeomPoint X=287.033 Y=168.845 Z=0
    g7: GeomPoint X=293.528 Y=172.595 Z=0
    g8: ArcOfCircle CenterX=1.26657 CenterY=-621.999 CenterZ=0 NormalX=0 NormalY=0 NormalZ=1 AngleXU=0 Radius=862 StartAngle=1.25533 EndAngle=1.57227
    g9: LineSegment StartX=5.28e-14 StartY=220.8 StartZ=0 EndX=5.51e-14 EndY=240 EndZ=0
    g10: ArcOfCircle CenterX=0 CenterY=-641.2 CenterZ=0 NormalX=0 NormalY=0 NormalZ=1 AngleXU=0 Radius=862 StartAngle=1.25386 EndAngle=1.5708
    g11: LineSegment StartX=5.51e-14 StartY=240 StartZ=0 EndX=268.713 EndY=197.462 EndZ=0
    g12: LineSegment StartX=5.28e-14 StartY=220.8 StartZ=0 EndX=268.65 EndY=177.867 EndZ=0
    g13: ArcOfCircle CenterX=0 CenterY=-676.059 CenterZ=0 NormalX=0 NormalY=0 NormalZ=1 AngleXU=0 Radius=900.059 StartAngle=1.27733 EndAngle=1.5708
    g14: Circle CenterX=268.65 CenterY=177.867 CenterZ=0 NormalX=0 NormalY=0 NormalZ=1 AngleXU=0 Radius=4
    g15: LineSegment StartX=0 StartY=0 StartZ=0 EndX=301.632 EndY=174.148 EndZ=0
    g16: LineSegment StartX=0 StartY=0 StartZ=0 EndX=-15 EndY=25.9808 EndZ=0
    g17: ArcOfCircle CenterX=262.507 CenterY=178.449 CenterZ=0 NormalX=0 NormalY=0 NormalZ=1 AngleXU=0 Radius=20 StartAngle=0.698132 EndAngle=1.25533
    g18: LineSegment StartX=292.762 StartY=173.508 StartZ=0 EndX=277.828 EndY=191.305 EndZ=0
  constraints (51):
    c: Tangent(g17,g8) = -1.5708
    c: Vertical(g1)
    c: PointOnObject(g1,g-2)
    c: Angle(g2) = -2.61799
    c: Tangent(g2,g0) = 1.5708
    c: DistanceY(g1,g1) = 1
    c: Tangent(g3,g2) = 1.5708
    c: Radius(g3) = 1
    c: Equal(g3,g0)
    c: Coincident(g4,g1)
    c: Vertical(g4)
    c: Distance(g4) = 15
    c: Tangent(g5,g3) = 1.5708
    c: PointOnObject(g7,g2)
    c: PointOnObject(g6,g2)
    c: PointOnObject(g6,g5)
    c: Coincident(g8,g1)
    c: PointOnObject(g9,g-2)
    c: DistanceY(g9,g4) = 3.2
    c: Coincident(g9,g1)
    c: Radius(g8) = 862  'outer_r'
    c: Distance(g6,g7) = 7.5
    c: PointOnObject(g10,g-2)
    c: Coincident(g11,g1)
    c: Coincident(g11,g17)
    c: Coincident(g12,g10)
    c: Coincident(g12,g10)
    c: Equal(g10,g8)
    c: Equal(g12,g11)
    c: Coincident(g10,g9)
    c: PointOnObject(g13,g-2)
    c: Coincident(g13,g4)
    c: Tangent(g13,g5) = -1.5708
    c: Coincident(g14,g10)
    c: Tangent(g14,g5)
    c: Radius(g14) = 4
    c: Coincident(g15,g-1)
    c: Angle(g15) = 0.523599
    c: Distance(g6,g15) = 2.7076
    c: DistanceY(g1) = 240
    c: Coincident(g16,g15)
    c: Perpendicular(g15,g16)
    c: Distance(g7,g16) = 340.5
    c: Tangent(g18,g0) = -1.5708
    c: Angle(g18) = 2.26893
    c: Tangent(g17,g18) = -1.5708
    c: PointOnObject(g8,g-5)
    c: Radius(g17) = 20
    c: PointOnObject(g7,g18)
    c: Radius(g5) = 60
    c: Distance(g16) = 30
FEATURE [PartDesign::Pad] Pad014
  Direction = (0,0,1)
  Length = 3
  Length2 = 10
  Profile = -> Sketch109
  ReferenceAxis = -> Sketch109 [N_Axis]
  Suppressed = false
  Type = 0
FEATURE [PartDesign::Mirrored] Mirrored008
  BaseFeature = -> Pad014
  MirrorPlane = -> Sketch109 [V_Axis]
  Originals = -> [Pad014]
  Refine = true
  Suppressed = false
FEATURE [PartDesign::Pocket] Pocket055
  BaseFeature = -> Mirrored008
  Direction = (0,0,-1)
  Length = 5
  Length2 = 5
  Profile = -> Binder062
  Reversed = true
  Suppressed = false
  Type = 0
FEATURE [PartDesign::Body] Body021
  Group = -> [Binder061,Binder062,Sketch109,Pad014,Mirrored008,Pocket055]
  Origin = -> Origin029
  Placement = pos=(0,0,0) rot=(1,0,0;0.116239rad)
  Tip = -> Pocket055
FEATURE [PartDesign::FeaturePython] Bend030  # WARN: FeaturePython — macro-defined, semantics opaque (R4)
  AutoMiter = true
  BaseFeature = -> Pocket022
  BendType = 0
  LengthList = [10]
  LengthSpec = 0
  ReliefFactor = 0.7
  Suppressed = false
  UseReliefFactor = false
  angle = 90
  baseObject = -> Pocket022 [Edge44,Edge42]
  bendAList = [90]
  extend1 = 0
  extend2 = 0
  gap1 = 0
  gap2 = 0
  invert = false
  kfactor = 0.5
  length = 10
  maxExtendDist = 5
  minGap = 0.1
  minReliefGap = 1
  miterangle1 = 0
  miterangle2 = 0
  offset = 0
  radius = 2
  reliefType = 0
  reliefd = 1
  reliefw = 0.8
  sketchflip = false
  sketchinvert = false
  unfold = true
  expr: radius = BaseBend011.radius
FEATURE [Sketcher::SketchObject] Sketch219
  AttachmentSupport = -> [Bend030]
  ExternalGeometry = -> [Bend030]
  FullyConstrained = true
  MapMode = 5
  Placement = pos=(0,-1.69e-14,1.483e-13) rot=(1,0,0;3.25479rad)
  sketch-geometry (6):
    g0: LineSegment StartX=297.803 StartY=-177.345 StartZ=0 EndX=303.917 EndY=-182.504 EndZ=0
    g1: LineSegment StartX=303.917 StartY=-182.504 StartZ=0 EndX=285.803 EndY=-203.969 EndZ=0
    g2: LineSegment StartX=285.803 StartY=-203.969 StartZ=0 EndX=276.608 EndY=-196.209 EndZ=0
    g3: LineSegment StartX=279.192 StartY=-196.205 StartZ=0 EndX=297.807 EndY=-180.398 EndZ=0
    g4: ArcOfCircle CenterX=296.513 CenterY=-178.873 CenterZ=0 NormalX=0 NormalY=0 NormalZ=1 AngleXU=0 Radius=2 StartAngle=5.41641 EndAngle=7.15307
    g5: ArcOfCircle CenterX=277.898 CenterY=-194.681 CenterZ=0 NormalX=0 NormalY=0 NormalZ=1 AngleXU=0 Radius=2 StartAngle=4.01147 EndAngle=5.41641
  constraints (15):
    c: Coincident(g0,g-3)
    c: Coincident(g0,g1)
    c: Coincident(g1,g-3)
    c: Coincident(g1,g2)
    c: Perpendicular(g1,g2)
    c: Perpendicular(g0,g1)
    c: Tangent(g4,g0) = 1.5708
    c: Tangent(g5,g2) = 1.5708
    c: Tangent(g5,g3) = -1.5708
    c: Tangent(g4,g3) = -1.5708
    c: Equal(g4,g5)
    c: Radius(g4) = 2
    c: Distance(g0) = 8
    c: Distance(g2) = 12.0319
    c: Distance(g3,g1) = 10.0593
FEATURE [PartDesign::Pocket] Pocket131
  BaseFeature = -> Bend030
  Direction = (0,-0.11295,0.993601)
  Length = 5
  Length2 = 5
  Profile = -> Sketch219
  ReferenceAxis = -> Sketch219 [N_Axis]
  Suppressed = false
  Type = 0
FEATURE [PartDesign::Mirrored] Mirrored017
  BaseFeature = -> Pocket131
  MirrorPlane = -> YZ_Plane028
  Originals = -> [Pocket131]
  Suppressed = false
FEATURE [PartDesign::Pocket] Pocket024
  BaseFeature = -> Mirrored017
  Direction = (0,0,-1)
  Length = 5
  Length2 = 5
  Midplane = true
  Profile = -> Sketch042
  ReferenceAxis = -> Sketch042 [N_Axis]
  Suppressed = false
  Type = 1
FEATURE [PartDesign::FeaturePython] CornerRelief  # WARN: FeaturePython — macro-defined, semantics opaque (R4)
  BaseFeature = -> Pocket024
  ReliefSketch = 0
  Size = 6
  SizeRatio = 1.5
  Sketch = -> Sketch043
  Suppressed = false
  XOffset = 0
  YOffset = 0
  baseObject = -> Pocket024 [Edge28,Edge31]
  kfactor = 0.5
FEATURE [PartDesign::Pocket] Pocket023
  BaseFeature = -> CornerRelief
  Direction = (-0.5,0.866025,-1e-16)
  Length = 0.6
  Length2 = 5
  Profile = -> Sketch041
  ReferenceAxis = -> Sketch041 [N_Axis]
  Suppressed = false
  Type = 0
FEATURE [PartDesign::Mirrored] Mirrored002
  BaseFeature = -> Pocket023
  MirrorPlane = -> YZ_Plane028
  Originals = -> [Pocket023]
  Refine = true
  Suppressed = false
FEATURE [PartDesign::Boolean] Boolean008
  BaseFeature = -> Mirrored002
  Group = -> [Compound028]
  Suppressed = false
  Type = 1
  UsePlacement = false
  expr: Group = <<sink_fix001>>._self
FEATURE [PartDesign::Pocket] Pocket029
  BaseFeature = -> Boolean008
  Direction = (0,0.11295,-0.993601)
  Length = 5
  Length2 = 5
  Profile = -> Sketch064
  ReferenceAxis = -> Sketch064 [N_Axis]
  Reversed = true
  Suppressed = false
  Type = 1
FEATURE [PartDesign::Body] Body020  label="sink_material_0.30ansi"
  Group = -> [Sketch037,Line,DatumLine,Sketch038,DatumLine001,Sketch039,BaseBend011,Bend004,Local_CS,Sketch040,Binder031,Pocket022,Sketch041,Sketch042,Bend030,Sketch219,Pocket131,Mirrored017,Pocket024,Sketch043,CornerRelief,Pocket023,Mirrored002,Boolean008,Sketch064,Pocket029]
  Origin = -> Origin028
  Tip = -> Pocket029
COMPONENT P74 — recipe-attached ("hat", modeled in this document).
Construction recipe (the document's own serialized feature program — sketch geometry with constraints, then the solid features built on it; lengths are millimeters unless a unit is written):

FEATURE [PartDesign::SubShapeBinder] Binder039
  BindCopyOnChange = 0
  BindMode = 0
  ClaimChildren = true
  Context = -> Body075 [Binder039.]
  Fuse = false
  MakeFace = true
  OffsetFill = false
  OffsetIntersection = false
  OffsetJoinType = 0
  OffsetOpenResult = false
  PartialLoad = false
  Relative = false
  Support = -> [Array005]
  _Version = 2
FEATURE [PartDesign::Pad] Pad009
  Direction = (0,0,1)
  Length = 3
  Length2 = 10
  Profile = -> Binder039
  Suppressed = false
  Type = 0
FEATURE [PartDesign::SubShapeBinder] Binder040
  BindCopyOnChange = 0
  BindMode = 0
  ClaimChildren = true
  Context = -> Part010 [Body075.Binder040.]
  Fuse = false
  MakeFace = true
  OffsetFill = false
  OffsetIntersection = false
  OffsetJoinType = 0
  OffsetOpenResult = false
  PartialLoad = false
  Placement = pos=(0,382,0) rot=(0,0,1;3.14159rad)
  Relative = false
  Support = -> [Sketch066]
  _Version = 2
  expr: Support = Sketch066._self
FEATURE [PartDesign::Pocket] Pocket032
  BaseFeature = -> Pad009
  Direction = (0,0,-1)
  Length = 5
  Length2 = 5
  Midplane = true
  Profile = -> Binder040
  Suppressed = false
  Type = 1
FEATURE [PartDesign::SubShapeBinder] Binder041
  BindCopyOnChange = 0
  BindMode = 0
  ClaimChildren = true
  Context = -> Body076 [Binder041.]
  Fuse = false
  MakeFace = true
  OffsetFill = false
  OffsetIntersection = false
  OffsetJoinType = 0
  OffsetOpenResult = false
  PartialLoad = false
  Relative = false
  Support = -> [Array006]
  _Version = 2
FEATURE [PartDesign::Pad] Pad010
  Direction = (0,0,1)
  Length = 3
  Length2 = 10
  Profile = -> Binder041
  Suppressed = false
  Type = 0
FEATURE [Sketcher::SketchObject] Sketch072
  AttachmentSupport = -> [XY_Plane039]
  FullyConstrained = true
  MapMode = 5
  sketch-geometry (3):
    g0: Circle CenterX=122.567 CenterY=-102.846 CenterZ=0 NormalX=0 NormalY=0 NormalZ=1 AngleXU=0 Radius=15
    g1: Circle CenterX=-122.567 CenterY=-102.846 CenterZ=0 NormalX=0 NormalY=0 NormalZ=1 AngleXU=0 Radius=15
    g2: LineSegment StartX=0 StartY=0 StartZ=0 EndX=122.567 EndY=-102.846 EndZ=0
  constraints (7):
    c: Coincident(g2,g-1)
    c: Coincident(g2,g0)
    c: Angle(g2) = -0.698132
    c: Symmetric(g1,g0,g-2)
    c: Equal(g0,g1)
    c: Distance(g2) = 160
    c: Diameter(g0) = 30
FEATURE [PartDesign::Pocket] Pocket033
  BaseFeature = -> Pad010
  Direction = (0,0,-1)
  Length = 5
  Length2 = 5
  Midplane = true
  Profile = -> Sketch072
  ReferenceAxis = -> Sketch072 [N_Axis]
  Suppressed = false
  Type = 1
FEATURE [PartDesign::Body] Body076  label="hat_top"
  Group = -> [Binder041,Pad010,Sketch072,Pocket033]
  Origin = -> Origin039
  Placement = pos=(0,0,87) rot=(0,0,1;0rad)
  Tip = -> Pocket033
FEATURE [PartDesign::SubShapeBinder] Binder048
  BindCopyOnChange = 0
  BindMode = 0
  ClaimChildren = true
  Context = -> Part010 [Body078.Binder048.]
  Fuse = false
  MakeFace = true
  OffsetFill = false
  OffsetIntersection = false
  OffsetJoinType = 0
  OffsetOpenResult = false
  PartialLoad = false
  Relative = false
  Support = -> [Compound043]
  _Version = 2
FEATURE [PartDesign::FeaturePython] BaseBend022  # WARN: FeaturePython — macro-defined, semantics opaque (R4)
  BendSide = 1
  BendSketch = -> Binder048
  MidPlane = false
  Reverse = false
  Suppressed = false
  length = 96
  radius = 1
  thickness = 1.5
FEATURE [PartDesign::SubShapeBinder] Binder049
  BindCopyOnChange = 0
  BindMode = 0
  ClaimChildren = true
  Context = -> Part010 [Body078.Binder049.]
  Fuse = false
  MakeFace = false
  OffsetFill = false
  OffsetIntersection = false
  OffsetJoinType = 0
  OffsetOpenResult = false
  PartialLoad = false
  Placement = pos=(0,362,6) rot=(0.57735,0.57735,0.57735;2.0944rad)
  Relative = false
  Support = -> [Sketch073]
  _Version = 2
  expr: Support = Sketch073._self
FEATURE [PartDesign::Plane] DatumPlane003
  AttachmentOffset = pos=(0,0,0) rot=(0,1,0;0.523599rad)
  AttachmentSupport = -> [XZ_Plane043]
  Length = 648.977
  MapMode = 5
  Placement = pos=(0,0,0) rot=(0.935113,0.250563,0.250563;1.63783rad)
  ResizeMode = 0
  Width = 174.677
FEATURE [PartDesign::Hole] Hole010
  BaseFeature = -> BaseBend022
  CustomThreadClearance = 0
  Depth = 1303.68
  DepthType = 1
  Diameter = 3.4
  DrillForDepth = false
  DrillPoint = 1
  DrillPointAngle = 118
  HoleCutCountersinkAngle = 90
  HoleCutCustomValues = false
  HoleCutDepth = 0
  HoleCutDiameter = 6.1
  HoleCutType = 0
  ModelThread = false
  Profile = -> Binder049
  Reversed = true
  Suppressed = false
  Tapered = false
  TaperedAngle = 90
  ThreadClass = 0
  ThreadDepth = 1303.68
  ThreadDepthType = 0
  ThreadDirection = 0
  ThreadFit = 0
  ThreadSize = 0
  ThreadType = 0
  Threaded = false
  UseCustomThreadClearance = false
  expr: Diameter = <<Properties>>.rivet_d
FEATURE [Sketcher::SketchObject] Sketch081
  AttachmentOffset = pos=(0,0,0) rot=(0,1,0;-1.0472rad)
  AttachmentSupport = -> [XZ_Plane043]
  FullyConstrained = true
  MapMode = 5
  Placement = pos=(0,0,0) rot=(-0.774597,0.447214,0.447214;4.45971rad)
  expr: Constraints[2] = <<Properties>>.rivet_d
  sketch-geometry (1):
    g0: Circle CenterX=0 CenterY=19 CenterZ=0 NormalX=0 NormalY=0 NormalZ=1 AngleXU=0 Radius=1.7
  constraints (3):
    c: PointOnObject(g0,g-2)
    c: DistanceY(g0) = 19
    c: Diameter(g0) = 3.4
FEATURE [PartDesign::Mirrored] Mirrored005
  BaseFeature = -> Hole010
  MirrorPlane = -> DatumPlane003
  Originals = -> [Hole010]
  Refine = true
  Suppressed = false
FEATURE [PartDesign::SubShapeBinder] Binder050
  BindCopyOnChange = 0
  BindMode = 0
  ClaimChildren = true
  Context = -> Part010 [Body078.Binder050.]
  Fuse = false
  MakeFace = true
  OffsetFill = false
  OffsetIntersection = false
  OffsetJoinType = 0
  OffsetOpenResult = false
  PartialLoad = false
  Relative = false
  Support = -> [Body075[Binder039.Array005.Compound039.Sketch068.]]
  _Version = 2
FEATURE [Sketcher::SketchObject] Sketch082
  AttachmentSupport = -> [XY_Plane043]
  FullyConstrained = true
  MapMode = 5
FEATURE [Sketcher::SketchObject] Sketch098
  AttachmentSupport = -> [XY_Plane038]
  FullyConstrained = true
  MapMode = 5
  sketch-geometry (1):
    g0: Circle CenterX=0 CenterY=0 CenterZ=0 NormalX=0 NormalY=0 NormalZ=1 AngleXU=0 Radius=3.25
  constraints (2):
    c: Coincident(g0,g-1)
    c: Diameter(g0) = 6.5
FEATURE [PartDesign::SubShapeBinder] Binder054  label="socket_fixture"
  BindCopyOnChange = 0
  BindMode = 0
  ClaimChildren = false
  Context = -> Part010 [Body075.Binder054.]
  Fuse = false
  MakeFace = true
  OffsetFill = false
  OffsetIntersection = false
  OffsetJoinType = 0
  OffsetOpenResult = false
  PartialLoad = false
  Placement = pos=(69,65,0) rot=(0,0,1;3.14159rad)
  Relative = false
  Support = -> [<external socket_fixture.FCStd>#Sketch003]
  _Version = 2
  expr: Support = socket_fixture#<<fix_holes>>._self
FEATURE [PartDesign::SubShapeBinder] Binder055  label="driver_fixture"
  BindCopyOnChange = 0
  BindMode = 0
  ClaimChildren = false
  Context = -> Part010 [Body075.Binder055.]
  Fuse = false
  MakeFace = true
  OffsetFill = false
  OffsetIntersection = false
  OffsetJoinType = 0
  OffsetOpenResult = false
  PartialLoad = false
  Placement = pos=(-24,152,0) rot=(0,0,1;0rad)
  Relative = false
  Support = -> [<external UET-VAS-060A20_12V_IP20.FCStd>#Sketch001]
  _Version = 2
  expr: Support = <<UET-VAS-060A20_12V_IP20>>#<<holes>>._self
FEATURE [Sketcher::SketchObject] Sketch108
  AttachmentSupport = -> [XY_Plane038]
  ExternalGeometry = -> [Binder039]
  FullyConstrained = true
  MapMode = 5
  expr: Constraints[3] = <<Properties>>.rivet_d
  sketch-geometry (2):
    g0: LineSegment StartX=112.627 StartY=65.0251 StartZ=0 EndX=101.801 EndY=58.7751 EndZ=0
    g1: Circle CenterX=101.801 CenterY=58.7751 CenterZ=0 NormalX=0 NormalY=0 NormalZ=1 AngleXU=0 Radius=1.7
  constraints (5):
    c: Coincident(g0,g-3)
    c: PointOnObject(g-1,g0)
    c: Coincident(g1,g0)
    c: Diameter(g1) = 3.4
    c: Distance(g0) = 12.5
FEATURE [PartDesign::Pocket] Pocket054
  BaseFeature = -> Pocket032
  Direction = (0,0,-1)
  Length = 5
  Length2 = 5
  Profile = -> Sketch108
  ReferenceAxis = -> Sketch108 [N_Axis]
  Reversed = true
  Suppressed = false
  Type = 0
FEATURE [PartDesign::PolarPattern] PolarPattern
  Angle = 360
  Axis = -> Z_Axis038
  BaseFeature = -> Pocket054
  Mode = 0
  Occurrences = 3
  Offset = 120
  Originals = -> [Pocket032,Pocket054]
  Suppressed = false
FEATURE [PartDesign::Hole] Hole015
  BaseFeature = -> PolarPattern
  CustomThreadClearance = 0
  Depth = 25
  DepthType = 0
  Diameter = 27.5
  DrillForDepth = false
  DrillPoint = 1
  DrillPointAngle = 118
  HoleCutCountersinkAngle = 90
  HoleCutCustomValues = false
  HoleCutDepth = 0
  HoleCutDiameter = 0
  HoleCutType = 0
  ModelThread = false
  Profile = -> Sketch098
  Reversed = true
  Suppressed = false
  Tapered = false
  TaperedAngle = 90
  ThreadClass = 0
  ThreadDepth = 23.5
  ThreadDepthType = 0
  ThreadDirection = 0
  ThreadFit = 0
  ThreadSize = 0
  ThreadType = 0
  Threaded = false
  UseCustomThreadClearance = false
  expr: Diameter = <<sleeve_inner_sketch>>.Constraints.outer_r * 2 + 1.5 mm
FEATURE [PartDesign::Hole] Hole016
  BaseFeature = -> Hole015
  CustomThreadClearance = 0
  Depth = 25
  DepthType = 0
  Diameter = 3.4
  DrillForDepth = false
  DrillPoint = 1
  DrillPointAngle = 118
  HoleCutCountersinkAngle = 90
  HoleCutCustomValues = false
  HoleCutDepth = 0
  HoleCutDiameter = 0
  HoleCutType = 0
  ModelThread = false
  Profile = -> Binder054
  Reversed = true
  Suppressed = false
  Tapered = false
  TaperedAngle = 90
  ThreadClass = 0
  ThreadDepth = 23.5
  ThreadDepthType = 0
  ThreadDirection = 0
  ThreadFit = 0
  ThreadSize = 0
  ThreadType = 0
  Threaded = false
  UseCustomThreadClearance = false
  expr: Diameter = <<Properties>>.rivet_d
FEATURE [PartDesign::Hole] Hole017
  BaseFeature = -> Hole016
  CustomThreadClearance = 0
  Depth = 25
  DepthType = 0
  Diameter = 3.4
  DrillForDepth = false
  DrillPoint = 1
  DrillPointAngle = 118
  HoleCutCountersinkAngle = 90
  HoleCutCustomValues = false
  HoleCutDepth = 0
  HoleCutDiameter = 0
  HoleCutType = 0
  ModelThread = false
  Profile = -> Binder055
  Reversed = true
  Suppressed = false
  Tapered = false
  TaperedAngle = 90
  ThreadClass = 0
  ThreadDepth = 23.5
  ThreadDepthType = 0
  ThreadDirection = 0
  ThreadFit = 0
  ThreadSize = 0
  ThreadType = 0
  Threaded = false
  UseCustomThreadClearance = false
FEATURE [PartDesign::Mirrored] Mirrored006
  BaseFeature = -> Hole017
  MirrorPlane = -> YZ_Plane038
  Originals = -> [Hole016]
  Refine = true
  Suppressed = false
FEATURE [PartDesign::Pocket] Pocket117
  BaseFeature = -> Mirrored005
  Direction = (0.866025,0.5,-1e-16)
  Length = 5
  Length2 = 5
  Midplane = true
  Profile = -> Sketch081
  ReferenceAxis = -> Sketch081 [N_Axis]
  Refine = true
  Suppressed = false
  Type = 1
FEATURE [PartDesign::Body] Body078  label="hat_plexiglass_material_0.30ansi"
  Group = -> [Binder048,BaseBend022,Binder049,DatumPlane003,Hole010,Sketch081,Mirrored005,Binder050,Sketch082,Pocket117]
  Origin = -> Origin043
  Placement = pos=(0,0,-3) rot=(0,0,1;0rad)
  Tip = -> Pocket117
FEATURE [PartDesign::SubShapeBinder] Binder135
  BindCopyOnChange = 0
  BindMode = 0
  ClaimChildren = false
  Context = -> Part010 [Body075.Binder135.]
  Fuse = false
  MakeFace = true
  OffsetFill = false
  OffsetIntersection = false
  OffsetJoinType = 0
  OffsetOpenResult = false
  PartialLoad = false
  Placement = pos=(35,150,0) rot=(0,0,1;0rad)
  Relative = false
  Support = -> [Sketch226]
  _Version = 2
  expr: Support = <<UV_driver_holder_holes_Sketch>>._self
FEATURE [PartDesign::Hole] Hole
  BaseFeature = -> Mirrored006
  CustomThreadClearance = 0
  Depth = 25
  DepthType = 0
  Diameter = 3.4
  DrillForDepth = false
  DrillPoint = 1
  DrillPointAngle = 118
  HoleCutCountersinkAngle = 90
  HoleCutCustomValues = false
  HoleCutDepth = 0
  HoleCutDiameter = 6.1
  HoleCutType = 0
  ModelThread = false
  Profile = -> Binder135
  Reversed = true
  Suppressed = false
  Tapered = false
  TaperedAngle = 90
  ThreadClass = 0
  ThreadDepth = 25
  ThreadDepthType = 0
  ThreadDirection = 0
  ThreadFit = 0
  ThreadSize = 0
  ThreadType = 0
  Threaded = false
  UseCustomThreadClearance = false
  expr: Diameter = <<Properties>>.rivet_d
FEATURE [PartDesign::Boolean] Boolean035
  BaseFeature = -> Hole
  Group = -> [Compound084]
  Suppressed = false
  Type = 1
  UsePlacement = false
FEATURE [PartDesign::Body] Body075  label="hat_bottom_material_0.30ansi"
  Group = -> [Binder039,Pad009,Binder040,Pocket032,Pocket054,PolarPattern,Sketch098,Hole015,Binder054,Binder055,Hole016,Hole017,Mirrored006,Sketch108,Binder135,Hole,Boolean035]
  Origin = -> Origin038
  Tip = -> Boolean035
COMPONENT P75 — geometry summary ("door3_2"; no construction recipe available for this part):
  bounding box: 1200.0 x 278.8 x 118.7 mm
  tessellated surface: 7,116 triangles
  volume: 348233 mm^3 (1% of its bounding box)
COMPONENT P76 — recipe-attached ("pillar2", modeled in this document).
Construction recipe (the document's own serialized feature program — sketch geometry with constraints, then the solid features built on it; lengths are millimeters unless a unit is written):

FEATURE [Sketcher::SketchObject] Sketch180
  AttachmentSupport = -> [YZ_Plane085]
  FullyConstrained = true
  MapMode = 5
  Placement = pos=(0,0,0) rot=(0.57735,0.57735,0.57735;2.0944rad)
  sketch-geometry (4):
    g0: ArcOfCircle CenterX=-4 CenterY=4 CenterZ=0 NormalX=0 NormalY=0 NormalZ=1 AngleXU=0 Radius=4 StartAngle=4.71239 EndAngle=6.28319
    g1: ArcOfCircle CenterX=-4 CenterY=4 CenterZ=0 NormalX=0 NormalY=0 NormalZ=1 AngleXU=0 Radius=2 StartAngle=4.71239 EndAngle=6.28319
    g2: LineSegment StartX=-4 StartY=0 StartZ=0 EndX=-4 EndY=2 EndZ=0
    g3: LineSegment StartX=-2 StartY=4 StartZ=0 EndX=0 EndY=4 EndZ=0
  constraints (13):
    c: PointOnObject(g0,g-1)
    c: PointOnObject(g0,g-2)
    c: Coincident(g1,g0)
    c: Coincident(g2,g0)
    c: Coincident(g2,g1)
    c: Coincident(g3,g1)
    c: Coincident(g3,g0)
    c: Perpendicular(g1,g3)
    c: Perpendicular(g1,g2)
    c: Vertical(g2)
    c: Horizontal(g3)
    c: Radius(g1) = 2  'r'
    c: Distance(g2) = 2  'thickness'
FEATURE [PartDesign::Pad] Pad020
  Direction = (1,-2e-16,3e-16)
  Length = 101
  Length2 = 10
  Midplane = true
  Placement = pos=(0,0,0) rot=(0.57735,0.57735,0.57735;2.0944rad)
  Profile = -> Sketch180
  ReferenceAxis = -> Sketch180 [N_Axis]
  Suppressed = false
  Type = 0
FEATURE [Sketcher::SketchObject] Sketch181
  AttachmentSupport = -> [XY_Plane085]
  FullyConstrained = true
  MapMode = 5
  expr: Constraints[2] = Pad020.Length
  sketch-geometry (4):
    g0: LineSegment StartX=-50.5 StartY=-4 StartZ=0 EndX=50.5 EndY=-4 EndZ=0
    g1: LineSegment StartX=29.5 StartY=-25 StartZ=0 EndX=-29.5 EndY=-25 EndZ=0
    g2: ArcOfCircle CenterX=29.5 CenterY=-4 CenterZ=0 NormalX=0 NormalY=0 NormalZ=1 AngleXU=0 Radius=21 StartAngle=4.71239 EndAngle=6.28319
    g3: ArcOfCircle CenterX=-29.5 CenterY=-4 CenterZ=0 NormalX=0 NormalY=0 NormalZ=1 AngleXU=0 Radius=21 StartAngle=3.14159 EndAngle=4.71239
  constraints (11):
    c: Horizontal(g1)
    c: DistanceY(g0) = -4
    c: DistanceX(g0,g0) = 101
    c: DistanceY(g1,g-1) = 25
    c: PointOnObject(g2,g0)
    c: Coincident(g2,g0)
    c: PointOnObject(g3,g0)
    c: Coincident(g3,g0)
    c: Tangent(g3,g1) = 1.5708
    c: Tangent(g2,g1) = 1.5708
    c: Symmetric(g0,g0,g-2)
FEATURE [Sketcher::SketchObject] Sketch182
  AttachmentSupport = -> [XZ_Plane085]
  FullyConstrained = true
  MapMode = 5
  Placement = pos=(0,0,0) rot=(1,0,0;1.5708rad)
  expr: Constraints[17] = <<pillar2_base_sketch>>.Constraints.length + 3 mm
  expr: Constraints[8] = Pad020.Length
  sketch-geometry (13):
    g0: LineSegment StartX=-50.5 StartY=4 StartZ=0 EndX=-50.5 EndY=110 EndZ=0
    g1: LineSegment StartX=-35.5 StartY=110 StartZ=0 EndX=-35.5 EndY=66.1722 EndZ=0
    g2: LineSegment StartX=-18.1011 StartY=38.947 StartZ=0 EndX=47.6002 EndY=8.53754 EndZ=0
    g3: ArcOfCircle CenterX=45.5 CenterY=4 CenterZ=0 NormalX=0 NormalY=0 NormalZ=1 AngleXU=0 Radius=5 StartAngle=2.92426e-11 EndAngle=1.13731
    g4: ArcOfCircle CenterX=-5.5 CenterY=66.1722 CenterZ=0 NormalX=0 NormalY=0 NormalZ=1 AngleXU=0 Radius=30 StartAngle=3.14159 EndAngle=4.27891
    g5: GeomPoint X=-35.5 Y=47 Z=0
    g6: GeomPoint X=-35.5 Y=110 Z=0
    g7: GeomPoint X=-52.5 Y=110 Z=0
    g8: LineSegment StartX=50.5 StartY=4 StartZ=0 EndX=-48.5 EndY=4 EndZ=0
    g9: LineSegment StartX=-48.5 StartY=4 StartZ=0 EndX=-50.5 EndY=4 EndZ=0
    g10: LineSegment StartX=-50.5 StartY=110 StartZ=0 EndX=-48.5 EndY=110 EndZ=0
    g11: LineSegment StartX=-48.5 StartY=110 StartZ=0 EndX=-35.5 EndY=110 EndZ=0
    g12: LineSegment StartX=-48.5 StartY=4 StartZ=0 EndX=-48.5 EndY=110 EndZ=0
  constraints (32):
    c: Vertical(g0)
    c: Coincident(g0,g10)
    c: Vertical(g1)
    c: Coincident(g9,g0)
    c: Coincident(g3,g8)
    c: Tangent(g3,g2) = 1.5708
    c: DistanceY(g8) = 4
    c: Symmetric(g0,g8,g-2)
    c: DistanceX(g9,g8) = 101
    c: DistanceY(g0) = 110  'total_height'
    c: PointOnObject(g5,g1)
    c: PointOnObject(g5,g2)
    c: Tangent(g1,g4) = -1.5708
    c: Tangent(g2,g4) = -1.5708
    c: Radius(g4) = 30
    c: Radius(g3) = 5
    c: DistanceX(g7,g0) = 2
    c: DistanceX(g7,g6) = 17
    c: Coincident(g8,g9)
    c: PointOnObject(g3,g8)
    c: Coincident(g10,g11)
    c: Horizontal(g10)
    c: Horizontal(g11)
    c: PointOnObject(g7,g10)
    c: Coincident(g12,g8)
    c: Coincident(g12,g11)
    c: Vertical(g12)
    c: DistanceX(g0,g11) = 2
    c: Horizontal(g9)
    c: DistanceY(g5) = 47
    c: Coincident(g1,g11)
    c: Coincident(g1,g6)
FEATURE [PartDesign::Pad] Pad021
  BaseFeature = -> Pad020
  Direction = (0,0,1)
  Length = 2
  Length2 = 10
  Placement = pos=(0,0,0) rot=(0.57735,0.57735,0.57735;2.0944rad)
  Profile = -> Sketch181
  ReferenceAxis = -> Sketch181 [N_Axis]
  Suppressed = false
  Type = 0
FEATURE [PartDesign::Pad] Pad022
  BaseFeature = -> Pad021
  Direction = (0,-1,-2e-16)
  Length = 2
  Length2 = 10
  Placement = pos=(0,0,0) rot=(0.57735,0.57735,0.57735;2.0944rad)
  Profile = -> Sketch182
  ReferenceAxis = -> Sketch182 [N_Axis]
  Suppressed = false
  Type = 0
FEATURE [Sketcher::SketchObject] Sketch183
  AttachmentOffset = pos=(-52.5,2,0) rot=(0,0,1;0rad)
  AttachmentSupport = -> [XY_Plane085]
  FullyConstrained = true
  MapMode = 5
  Placement = pos=(-52.5,2,0) rot=(0,0,1;0rad)
  expr: .AttachmentOffset.Base.x = -Pad020.Length / 2 - 2 mm
  expr: Constraints[16] = <<pillar2_base_sketch>>.Constraints.width / 2 - 1 mm
  sketch-geometry (9):
    g0: ArcOfCircle CenterX=-5.92e-14 CenterY=4.503e-13 CenterZ=0 NormalX=0 NormalY=0 NormalZ=1 AngleXU=0 Radius=2 StartAngle=3.14159 EndAngle=4.71239
    g1: ArcOfCircle CenterX=-5.92e-14 CenterY=4.503e-13 CenterZ=0 NormalX=0 NormalY=0 NormalZ=1 AngleXU=0 Radius=4 StartAngle=3.14159 EndAngle=4.71239
    g2: LineSegment StartX=-2 StartY=-4.469e-13 StartZ=0 EndX=-2 EndY=15.3 EndZ=0
    g3: LineSegment StartX=-2 StartY=15.3 StartZ=0 EndX=-4 EndY=15.3 EndZ=0
    g4: LineSegment StartX=-4 StartY=15.3 StartZ=0 EndX=-4 EndY=0 EndZ=0
    g5: LineSegment StartX=0 StartY=-4 StartZ=0 EndX=0 EndY=-2 EndZ=0
    g6: LineSegment StartX=0 StartY=-4 StartZ=0 EndX=2 EndY=-4 EndZ=0
    g7: LineSegment StartX=2 StartY=-4 StartZ=0 EndX=2 EndY=-2 EndZ=0
    g8: LineSegment StartX=2 StartY=-2 StartZ=0 EndX=0 EndY=-2 EndZ=0
  constraints (25):
    c: Coincident(g0,g-1)
    c: PointOnObject(g0,g-2)
    c: PointOnObject(g0,g-1)
    c: Coincident(g1,g0)
    c: PointOnObject(g1,g-2)
    c: PointOnObject(g1,g-1)
    c: Tangent(g0,g2) = 1.5708
    c: Coincident(g2,g3)
    c: Horizontal(g3)
    c: Coincident(g3,g4)
    c: Coincident(g4,g1)
    c: Vertical(g4)
    c: Coincident(g5,g1)
    c: Coincident(g5,g0)
    c: Radius(g0) = 2
    c: DistanceY(g5,g5) = 2
    c: DistanceY(g0,g2) = 17.3
    c: Coincident(g6,g7)
    c: Coincident(g7,g8)
    c: Horizontal(g6)
    c: Horizontal(g8)
    c: Vertical(g7)
    c: Coincident(g6,g1)
    c: Coincident(g0,g8)
    c: DistanceX(g6,g6) = 2
FEATURE [Sketcher::SketchObject] Sketch184
  AttachmentSupport = -> [YZ_Plane085]
  ExternalGeometry = -> [Sketch183]
  FullyConstrained = true
  MapMode = 5
  Placement = pos=(0,0,0) rot=(0.57735,0.57735,0.57735;2.0944rad)
  expr: Constraints[12] = Sketch182.Constraints.total_height
  sketch-geometry (9):
    g0: ArcOfCircle CenterX=15.3 CenterY=2 CenterZ=0 NormalX=0 NormalY=0 NormalZ=1 AngleXU=0 Radius=2 StartAngle=4.71239 EndAngle=6.28319
    g1: LineSegment StartX=17.3 StartY=2 StartZ=0 EndX=17.3 EndY=1.47e-14 EndZ=0
    g2: LineSegment StartX=17.3 StartY=1.47e-14 StartZ=0 EndX=15.3 EndY=1.95e-14 EndZ=0
    g3: LineSegment StartX=17.3 StartY=108 StartZ=0 EndX=17.3 EndY=110 EndZ=0
    g4: LineSegment StartX=17.3 StartY=110 StartZ=0 EndX=15.3 EndY=110 EndZ=0
    g5: ArcOfCircle CenterX=15.3 CenterY=108 CenterZ=0 NormalX=0 NormalY=0 NormalZ=1 AngleXU=0 Radius=2 StartAngle=-5.3e-15 EndAngle=1.5708
    g6: ArcOfCircle CenterX=4 CenterY=2 CenterZ=0 NormalX=0 NormalY=0 NormalZ=1 AngleXU=0 Radius=2 StartAngle=3.14159 EndAngle=4.71239
    g7: LineSegment StartX=2 StartY=2 StartZ=0 EndX=2 EndY=1.11e-14 EndZ=0
    g8: LineSegment StartX=2 StartY=1.11e-14 StartZ=0 EndX=4 EndY=3.55e-14 EndZ=0
  constraints (22):
    c: Coincident(g1,g2)
    c: Vertical(g3)
    c: Coincident(g3,g4)
    c: Horizontal(g4)
    c: Tangent(g5,g4) = -1.5708
    c: Tangent(g5,g3) = -1.5708
    c: Vertical(g1)
    c: Tangent(g0,g1) = 1.5708
    c: Tangent(g2,g0) = 1.5708
    c: Vertical(g3,g1)
    c: Equal(g5,g0)
    c: Radius(g5) = 2
    c: DistanceY(g3) = 110
    c: Coincident(g7,g8)
    c: Vertical(g7)
    c: Tangent(g6,g7) = -1.5708
    c: Tangent(g8,g6) = -1.5708
    c: Equal(g6,g0)
    c: Coincident(g1,g-3)
    c: Coincident(g7,g-3)
    c: PointOnObject(g6,g-3)
    c: PointOnObject(g0,g-1)
FEATURE [Sketcher::SketchObject] Sketch185
  AttachmentOffset = pos=(-52.5,2,0) rot=(0,0,1;0rad)
  AttachmentSupport = -> [XY_Plane085]
  FullyConstrained = true
  MapMode = 5
  Placement = pos=(-52.5,2,0) rot=(0,0,1;0rad)
  expr: AttachmentOffset = <<Sketch183>>.AttachmentOffset
  sketch-geometry (6):
    g0: ArcOfCircle CenterX=-1.4879e-12 CenterY=3.7497e-12 CenterZ=0 NormalX=0 NormalY=0 NormalZ=1 AngleXU=0 Radius=4 StartAngle=3.14159 EndAngle=4.71239
    g1: ArcOfCircle CenterX=-1.4879e-12 CenterY=3.7497e-12 CenterZ=0 NormalX=0 NormalY=0 NormalZ=1 AngleXU=0 Radius=2 StartAngle=3.14159 EndAngle=4.71239
    g2: LineSegment StartX=-4 StartY=-4.94e-14 StartZ=0 EndX=-2 EndY=-2.158e-13 EndZ=0
    g3: LineSegment StartX=1.0947e-12 StartY=-4 StartZ=0 EndX=2 EndY=-4 EndZ=0
    g4: LineSegment StartX=2 StartY=-4 StartZ=0 EndX=2 EndY=-2 EndZ=0
    g5: LineSegment StartX=2 StartY=-2 StartZ=0 EndX=1.583e-13 EndY=-2 EndZ=0
  constraints (17):
    c: Coincident(g0,g-1)
    c: PointOnObject(g0,g-2)
    c: PointOnObject(g0,g-1)
    c: Coincident(g1,g0)
    c: PointOnObject(g1,g-2)
    c: PointOnObject(g1,g-1)
    c: Coincident(g2,g0)
    c: Coincident(g2,g1)
    c: Radius(g1) = 2
    c: Radius(g0) = 4
    c: Tangent(g0,g3) = -1.5708
    c: Coincident(g3,g4)
    c: Vertical(g4)
    c: Coincident(g4,g5)
    c: Coincident(g5,g1)
    c: Horizontal(g5)
    c: DistanceX(g5,g5) = 2
FEATURE [Sketcher::SketchObject] Sketch186  label="pillar2_base_sketch"
  AttachmentSupport = -> [XY_Plane086]
  FullyConstrained = true
  MapMode = 5
  expr: .Constraints.length = <<pillar2_Properties>>.outer_length
  sketch-geometry (5):
    g0: LineSegment StartX=-18.3 StartY=14 StartZ=0 EndX=-18.3 EndY=0 EndZ=0
    g1: LineSegment StartX=-18.3 StartY=0 StartZ=0 EndX=18.3 EndY=0 EndZ=0
    g2: LineSegment StartX=18.3 StartY=0 StartZ=0 EndX=18.3 EndY=14 EndZ=0
    g3: LineSegment StartX=18.3 StartY=14 StartZ=0 EndX=-18.3 EndY=14 EndZ=0
    g4: GeomPoint X=0 Y=7 Z=0
  constraints (13):
    c: Coincident(g0,g1)
    c: Coincident(g1,g2)
    c: Coincident(g2,g3)
    c: Coincident(g3,g0)
    c: Horizontal(g1)
    c: Horizontal(g3)
    c: Vertical(g0)
    c: Vertical(g2)
    c: Symmetric(g1,g0,g4)
    c: PointOnObject(g4,g-2)
    c: PointOnObject(g1,g-1)
    c: DistanceX(g1,g1) = 36.6  'width'
    c: DistanceY(g2,g2) = 14  'length'
FEATURE [PartDesign::FeaturePython] BaseBend045  # WARN: FeaturePython — macro-defined, semantics opaque (R4)
  BendSide = 1
  BendSketch = -> Sketch186
  MidPlane = false
  Reverse = false
  Suppressed = false
  length = 1596
  radius = 2
  thickness = 2
FEATURE [Sketcher::SketchObject] Sketch187
  AttachmentOffset = pos=(0,1598,0) rot=(0,0,1;0rad)
  AttachmentSupport = -> [XZ_Plane086]
  FullyConstrained = true
  MapMode = 5
  Placement = pos=(0,3.548e-13,1598) rot=(1,0,0;1.5708rad)
  expr: .AttachmentOffset.Base.y = BaseBend045.length + Sketch188.Constraints.length
  expr: Constraints[11] = <<pillar2_Properties>>.outer_width - 4 mm * 2 + (<<pillar2_Properties>>.outer_length - 4 mm) * 2 + 9.42 mm
  sketch-geometry (5):
    g0: LineSegment StartX=-29.01 StartY=88 StartZ=0 EndX=-29.01 EndY=0 EndZ=0
    g1: LineSegment StartX=-29.01 StartY=0 StartZ=0 EndX=29.01 EndY=0 EndZ=0
    g2: LineSegment StartX=29.01 StartY=0 StartZ=0 EndX=29.01 EndY=88 EndZ=0
    g3: LineSegment StartX=29.01 StartY=88 StartZ=0 EndX=-29.01 EndY=88 EndZ=0
    g4: GeomPoint X=0 Y=44 Z=0
  constraints (13):
    c: Coincident(g0,g1)
    c: Coincident(g1,g2)
    c: Coincident(g2,g3)
    c: Coincident(g3,g0)
    c: Horizontal(g1)
    c: Horizontal(g3)
    c: Vertical(g0)
    c: Vertical(g2)
    c: Symmetric(g1,g0,g4)
    c: PointOnObject(g4,g-2)
    c: PointOnObject(g1,g-1)
    c: DistanceX(g1,g1) = 58.02
    c: DistanceY(g2,g2) = 88
FEATURE [Sketcher::SketchObject] Sketch188
  AttachmentOffset = pos=(0,1596,0) rot=(0,0,1;0rad)
  AttachmentSupport = -> [XZ_Plane086]
  FullyConstrained = true
  MapMode = 5
  Placement = pos=(0,3.544e-13,1596) rot=(1,0,0;1.5708rad)
  expr: .AttachmentOffset.Base.y = BaseBend045.length
  expr: Constraints[11] = <<pillar2_Properties>>.outer_width - (<<pillar2_Properties>>.thickness + <<pillar2_Properties>>.default_bend_r) * 2
  sketch-geometry (7):
    g0: LineSegment StartX=-14.3 StartY=2 StartZ=0 EndX=-14.3 EndY=-4e-16 EndZ=0
    g1: LineSegment StartX=-14.3 StartY=-4e-16 StartZ=0 EndX=14.3 EndY=-4e-16 EndZ=0
    g2: LineSegment StartX=14.3 StartY=-4e-16 StartZ=0 EndX=14.3 EndY=2 EndZ=0
    g3: LineSegment StartX=14.3 StartY=2 StartZ=0 EndX=-14.3 EndY=2 EndZ=0
    g4: GeomPoint X=-2.547e-12 Y=1 Z=0
    g5: ArcOfCircle CenterX=14.3 CenterY=1 CenterZ=0 NormalX=0 NormalY=0 NormalZ=1 AngleXU=0 Radius=1 StartAngle=1.5708 EndAngle=4.71239
    g6: ArcOfCircle CenterX=-14.3 CenterY=1 CenterZ=0 NormalX=0 NormalY=0 NormalZ=1 AngleXU=0 Radius=1 StartAngle=4.71239 EndAngle=7.85398
  constraints (19):
    c: Coincident(g0,g1)
    c: Coincident(g1,g2)
    c: Coincident(g2,g3)
    c: Coincident(g3,g0)
    c: Horizontal(g1)
    c: Horizontal(g3)
    c: Vertical(g0)
    c: Vertical(g2)
    c: Symmetric(g1,g0,g4)
    c: PointOnObject(g4,g-2)
    c: PointOnObject(g1,g-1)
    c: DistanceX(g1,g1) = 28.6
    c: DistanceY(g2) = 2  'length'
    c: PointOnObject(g5,g2)
    c: Coincident(g5,g1)
    c: Coincident(g5,g3)
    c: PointOnObject(g6,g0)
    c: Coincident(g6,g1)
    c: Coincident(g6,g3)
FEATURE [PartDesign::Pad] Pad024
  BaseFeature = -> BaseBend045
  Direction = (0,-1,2e-16)
  Length = 2
  Length2 = 10
  Profile = -> Sketch188
  ReferenceAxis = -> Sketch188 [N_Axis]
  Reversed = true
  Suppressed = false
  Type = 0
FEATURE [PartDesign::Pad] Pad025
  BaseFeature = -> Pad024
  Direction = (0,-1,2e-16)
  Length = 2
  Length2 = 10
  Profile = -> Sketch187
  ReferenceAxis = -> Sketch187 [N_Axis]
  Reversed = true
  Suppressed = false
  Type = 0
FEATURE [Sketcher::SketchObject] Sketch189
  AttachmentSupport = -> [XZ_Plane086]
  ExternalGeometry = -> [Sketch187]
  FullyConstrained = true
  MapMode = 5
  Placement = pos=(0,0,0) rot=(1,0,0;1.5708rad)
  sketch-geometry (12):
    g0: LineSegment StartX=26.01 StartY=1598 StartZ=0 EndX=29.01 EndY=1598 EndZ=0
    g1: LineSegment StartX=29.01 StartY=1598 StartZ=0 EndX=29.01 EndY=1601 EndZ=0
    g2: LineSegment StartX=29.01 StartY=1683 StartZ=0 EndX=29.01 EndY=1686 EndZ=0
    g3: LineSegment StartX=29.01 StartY=1686 StartZ=0 EndX=26.01 EndY=1686 EndZ=0
    g4: LineSegment StartX=-26.01 StartY=1686 StartZ=0 EndX=-29.01 EndY=1686 EndZ=0
    g5: LineSegment StartX=-29.01 StartY=1686 StartZ=0 EndX=-29.01 EndY=1683 EndZ=0
    g6: LineSegment StartX=-29.01 StartY=1601 StartZ=0 EndX=-29.01 EndY=1598 EndZ=0
    g7: LineSegment StartX=-29.01 StartY=1598 StartZ=0 EndX=-26.01 EndY=1598 EndZ=0
    g8: ArcOfCircle CenterX=26.01 CenterY=1601 CenterZ=0 NormalX=0 NormalY=0 NormalZ=1 AngleXU=0 Radius=3 StartAngle=4.71239 EndAngle=6.28319
    g9: ArcOfCircle CenterX=26.01 CenterY=1683 CenterZ=0 NormalX=0 NormalY=0 NormalZ=1 AngleXU=0 Radius=3 StartAngle=-2.04e-14 EndAngle=1.5708
    g10: ArcOfCircle CenterX=-26.01 CenterY=1683 CenterZ=0 NormalX=0 NormalY=0 NormalZ=1 AngleXU=0 Radius=3 StartAngle=1.5708 EndAngle=3.14159
    g11: ArcOfCircle CenterX=-26.01 CenterY=1601 CenterZ=0 NormalX=0 NormalY=0 NormalZ=1 AngleXU=0 Radius=3 StartAngle=3.14159 EndAngle=4.71239
  constraints (29):
    c: Coincident(g0,g-3)
    c: Horizontal(g0)
    c: Coincident(g0,g1)
    c: PointOnObject(g1,g-3)
    c: PointOnObject(g2,g-3)
    c: Coincident(g2,g-3)
    c: Coincident(g2,g3)
    c: Horizontal(g3)
    c: Coincident(g4,g-4)
    c: Horizontal(g4)
    c: Coincident(g4,g5)
    c: PointOnObject(g5,g-4)
    c: PointOnObject(g6,g-4)
    c: Coincident(g6,g-4)
    c: Coincident(g6,g7)
    c: Horizontal(g7)
    c: Coincident(g9,g3)
    c: Tangent(g8,g0) = -1.5708
    c: Tangent(g8,g1) = -1.5708
    c: Tangent(g9,g2) = -1.5708
    c: Tangent(g9,g3,g3) = -1.5708
    c: Tangent(g10,g4) = -1.5708
    c: Tangent(g10,g5) = -1.5708
    c: Tangent(g11,g7) = -1.5708
    c: Tangent(g11,g6) = -1.5708
    c: Equal(g8,g9)
    c: Equal(g8,g10)
    c: Equal(g8,g11)
    c: Radius(g8) = 3
FEATURE [PartDesign::Pocket] Pocket115
  BaseFeature = -> Pad025
  Direction = (0,1,-2e-16)
  Length = 5
  Length2 = 5
  Profile = -> Sketch189
  ReferenceAxis = -> Sketch189 [N_Axis]
  Suppressed = false
  Type = 1
FEATURE [Sketcher::SketchObject] Sketch190
  AttachmentOffset = pos=(14,0,0) rot=(0,0,1;0rad)
  AttachmentSupport = -> [YZ_Plane086]
  FullyConstrained = true
  MapMode = 5
  Placement = pos=(0,14,0) rot=(0.57735,0.57735,0.57735;2.0944rad)
  expr: .AttachmentOffset.Base.x = <<pillar2_Properties>>.outer_length
  sketch-geometry (3):
    g0: ArcOfCircle CenterX=-3 CenterY=3 CenterZ=0 NormalX=0 NormalY=0 NormalZ=1 AngleXU=0 Radius=3 StartAngle=4.71239 EndAngle=6.28319
    g1: LineSegment StartX=-5.6e-14 StartY=3 StartZ=0 EndX=-5.6e-14 EndY=0 EndZ=0
    g2: LineSegment StartX=-5.6e-14 StartY=0 StartZ=0 EndX=-3 EndY=6.7e-15 EndZ=0
  constraints (7):
    c: PointOnObject(g0,g-1)
    c: Coincident(g2,g1)
    c: Vertical(g1)
    c: Tangent(g0,g1) = 1.5708
    c: Tangent(g2,g0) = 1.5708
    c: Coincident(g1,g-1)
    c: Radius(g0) = 3
FEATURE [PartDesign::Pocket] Pocket116
  BaseFeature = -> Pocket115
  Direction = (-1,2e-16,-3e-16)
  Length = 5
  Length2 = 5
  Midplane = true
  Profile = -> Sketch190
  ReferenceAxis = -> Sketch190 [N_Axis]
  Suppressed = false
  Type = 1
FEATURE [PartDesign::Plane] DatumPlane006
  AttachmentOffset = pos=(0,0,798) rot=(1,0,0;0rad)
  AttachmentSupport = -> [XY_Plane086]
  Length = 68.7922
  MapMode = 5
  Placement = pos=(0,0,798) rot=(0,0,1;0rad)
  ResizeMode = 0
  Width = 60.7722
  expr: .AttachmentOffset.Base.z = BaseBend045.length / 2
FEATURE [PartDesign::Mirrored] Mirrored013
  BaseFeature = -> Pocket116
  MirrorPlane = -> DatumPlane006
  Originals = -> [Pocket116]
  Suppressed = false
FEATURE [Sketcher::SketchObject] Sketch192
  AttachmentSupport = -> [XZ_Plane085]
  FullyConstrained = true
  MapMode = 5
  Placement = pos=(0,0,0) rot=(1,0,0;1.5708rad)
  sketch-geometry (4):
    g0: LineSegment StartX=-46.5 StartY=-2.18e-14 StartZ=0 EndX=-50.5 EndY=-2.18e-14 EndZ=0
    g1: LineSegment StartX=-50.5 StartY=-2.18e-14 StartZ=0 EndX=-50.5 EndY=4 EndZ=0
    g2: LineSegment StartX=-50.5 StartY=4 StartZ=0 EndX=-46.5 EndY=4 EndZ=0
    g3: LineSegment StartX=-46.5 StartY=4 StartZ=0 EndX=-46.5 EndY=-2.18e-14 EndZ=0
  constraints (12):
    c: Coincident(g0,g1)
    c: Coincident(g1,g2)
    c: Coincident(g2,g3)
    c: Coincident(g3,g0)
    c: Horizontal(g0)
    c: Horizontal(g2)
    c: Vertical(g1)
    c: Vertical(g3)
    c: PointOnObject(g0,g-1)
    c: DistanceX(g0,g0) = 4
    c: Equal(g1,g0)
    c: DistanceX(g0) = -50.5
FEATURE [Sketcher::SketchObject] Sketch194
  AttachmentSupport = -> [XZ_Plane085]
  FullyConstrained = true
  MapMode = 5
  Placement = pos=(0,0,0) rot=(1,0,0;1.5708rad)
  sketch-geometry (6):
    g0: LineSegment StartX=-50.5 StartY=108 StartZ=0 EndX=-50.5 EndY=110 EndZ=0
    g1: LineSegment StartX=-50.5 StartY=110 StartZ=0 EndX=-48.5 EndY=110 EndZ=0
    g2: LineSegment StartX=-43.5 StartY=110 StartZ=0 EndX=-35.5 EndY=110 EndZ=0
    g3: LineSegment StartX=-35.5 StartY=110 StartZ=0 EndX=-35.5 EndY=102 EndZ=0
    g4: ArcOfCircle CenterX=-43.5 CenterY=102 CenterZ=0 NormalX=0 NormalY=0 NormalZ=1 AngleXU=0 Radius=8 StartAngle=8.302e-13 EndAngle=1.5708
    g5: ArcOfCircle CenterX=-48.5 CenterY=108 CenterZ=0 NormalX=0 NormalY=0 NormalZ=1 AngleXU=0 Radius=2 StartAngle=1.5708 EndAngle=3.14159
  constraints (16):
    c: Vertical(g0)
    c: Coincident(g0,g1)
    c: Horizontal(g1)
    c: Horizontal(g2)
    c: Coincident(g2,g3)
    c: Vertical(g3)
    c: Horizontal(g0,g2)
    c: DistanceY(g0) = 110
    c: Tangent(g5,g0) = 1.5708
    c: DistanceX(g0) = -50.5
    c: Tangent(g5,g1) = 1.5708
    c: Tangent(g4,g3) = 1.5708
    c: Tangent(g4,g2) = 1.5708
    c: DistanceX(g0,g2) = 15
    c: DistanceX(g0,g2) = 7
    c: Radius(g5) = 2
FEATURE [PartDesign::Pocket] Pocket119
  BaseFeature = -> Pad022
  Direction = (0,1,2e-16)
  Length = 5
  Length2 = 5
  Midplane = true
  Placement = pos=(0,0,0) rot=(0.57735,0.57735,0.57735;2.0944rad)
  Profile = -> Sketch194
  ReferenceAxis = -> Sketch194 [N_Axis]
  Suppressed = false
  Type = 1
FEATURE [PartDesign::Boolean] Boolean015
  BaseFeature = -> Pocket119
  Group = -> [Compound054]
  Refine = true
  Suppressed = false
  Type = 1
  UsePlacement = false
FEATURE [PartDesign::Body] Body111  label="pillar2_bottom_material_0.50ansi"
  Group = -> [Sketch180,Pad020,Sketch181,Sketch182,Sketch192,Pad021,Pad022,Sketch183,Sketch184,Sketch185,Pocket119,Boolean015,Sketch194]
  Origin = -> Origin085
  Placement = pos=(18.3,54.5,0) rot=(0,0,1;1.5708rad)
  Tip = -> Boolean015
FEATURE [PartDesign::Boolean] Boolean016
  BaseFeature = -> Mirrored013
  Group = -> [Compound052]
  Refine = true
  Suppressed = false
  Type = 1
  UsePlacement = false
FEATURE [PartDesign::Body] Body112  label="pillar2_material_0.50ansi"
  Group = -> [Sketch186,BaseBend045,Sketch187,Sketch188,Pad024,Pad025,Sketch189,Pocket115,Sketch190,Pocket116,DatumPlane006,Mirrored013,Boolean016]
  Origin = -> Origin086
  Tip = -> Boolean016
COMPONENT P77 — recipe-attached ("basement_v2", modeled in this document).
Construction recipe (the document's own serialized feature program — sketch geometry with constraints, then the solid features built on it; lengths are millimeters unless a unit is written):

FEATURE [PartDesign::SubShapeBinder] Binder123
  BindCopyOnChange = 0
  BindMode = 0
  ClaimChildren = true
  Context = -> Part020 [Body114.Binder123.]
  Fuse = false
  MakeFace = true
  OffsetFill = false
  OffsetIntersection = false
  OffsetJoinType = 0
  OffsetOpenResult = false
  PartialLoad = false
  Relative = true
  Support = -> [Array009]
  _Version = 2
FEATURE [PartDesign::Pad] Pad026
  Direction = (0,0,1)
  Length = 18
  Length2 = 10
  Profile = -> Binder123
  Suppressed = false
  Type = 0
FEATURE [Sketcher::SketchObject] Sketch199
  AttachmentSupport = -> [XY_Plane090]
  FullyConstrained = true
  MapMode = 5
  sketch-geometry (5):
    g0: LineSegment StartX=-42.5 StartY=-49 StartZ=0 EndX=-42.5 EndY=49 EndZ=0
    g1: LineSegment StartX=-42.5 StartY=49 StartZ=0 EndX=42.5 EndY=49 EndZ=0
    g2: LineSegment StartX=42.5 StartY=49 StartZ=0 EndX=42.5 EndY=-49 EndZ=0
    g3: LineSegment StartX=42.5 StartY=-49 StartZ=0 EndX=-42.5 EndY=-49 EndZ=0
    g4: GeomPoint X=0 Y=0 Z=0
  constraints (12):
    c: Coincident(g0,g1)
    c: Coincident(g1,g2)
    c: Coincident(g2,g3)
    c: Coincident(g3,g0)
    c: Horizontal(g1)
    c: Horizontal(g3)
    c: Vertical(g0)
    c: Vertical(g2)
    c: Symmetric(g1,g0,g4)
    c: Coincident(g4,g-1)
    c: DistanceX(g0,g1) = 85
    c: DistanceY(g0,g1) = 98
FEATURE [Sketcher::SketchObject] Sketch200
  AttachmentOffset = pos=(0,0,3) rot=(0,0,1;0rad)
  AttachmentSupport = -> [XY_Plane090]
  FullyConstrained = true
  MapMode = 5
  Placement = pos=(0,0,3) rot=(0,0,1;0rad)
  sketch-geometry (7):
    g0: LineSegment StartX=9.81495 StartY=3.2e-14 StartZ=0 EndX=4.90748 EndY=8.5 EndZ=0
    g1: LineSegment StartX=4.90748 StartY=8.5 StartZ=0 EndX=-4.90748 EndY=8.5 EndZ=0
    g2: LineSegment StartX=-4.90748 StartY=8.5 StartZ=0 EndX=-9.81495 EndY=-2.149e-13 EndZ=0
    g3: LineSegment StartX=-9.81495 StartY=-2.149e-13 StartZ=0 EndX=-4.90748 EndY=-8.5 EndZ=0
    g4: LineSegment StartX=-4.90748 StartY=-8.5 StartZ=0 EndX=4.90748 EndY=-8.5 EndZ=0
    g5: LineSegment StartX=4.90748 StartY=-8.5 StartZ=0 EndX=9.81495 EndY=3.2e-14 EndZ=0
    g6: Circle CenterX=2.6e-15 CenterY=-5.63e-14 CenterZ=0 NormalX=0 NormalY=0 NormalZ=1 AngleXU=0 Radius=9.81495
  constraints (16):
    c: Coincident(g0,g1)
    c: Coincident(g1,g2)
    c: Coincident(g2,g3)
    c: Coincident(g3,g4)
    c: Coincident(g4,g5)
    c: Coincident(g5,g0)
    c: Equal(g0, g1-g5) x5
    c: PointOnObject(g0,g6)
    c: PointOnObject(g1,g6)
    c: PointOnObject(g2,g6)
    c: PointOnObject(g3,g6)
    c: PointOnObject(g4,g6)
    c: PointOnObject(g5,g6)
    c: Coincident(g6,g-1)
    c: PointOnObject(g5,g-1)
    c: DistanceY(g4,g0) = 17
FEATURE [PartDesign::SubShapeBinder] Binder124
  BindCopyOnChange = 0
  BindMode = 0
  ClaimChildren = false
  Context = -> Part020 [Body116.Binder124.]
  Fuse = false
  MakeFace = true
  OffsetFill = false
  OffsetIntersection = false
  OffsetJoinType = 0
  OffsetOpenResult = false
  PartialLoad = false
  Relative = true
  Support = -> [Array003]
  _Version = 2
  expr: Support = Array003._self
FEATURE [PartDesign::Pad] Pad027
  Direction = (0,0,1)
  Length = 18
  Length2 = 10
  Profile = -> Binder124
  Suppressed = false
  Type = 0
FEATURE [PartDesign::Body] Body116  label="basement_v2_top"
  Group = -> [Binder124,Pad027]
  Origin = -> Origin091
  Tip = -> Pad027
FEATURE [PartDesign::SubShapeBinder] Binder125
  BindCopyOnChange = 0
  BindMode = 0
  ClaimChildren = true
  Context = -> Part020 [Body117.Binder125.]
  Fuse = false
  MakeFace = true
  OffsetFill = false
  OffsetIntersection = false
  OffsetJoinType = 0
  OffsetOpenResult = false
  PartialLoad = false
  Relative = false
  Support = -> [Array002]
  _Version = 2
FEATURE [PartDesign::Pad] Pad028
  Direction = (0,0,1)
  Length = 18
  Length2 = 10
  Profile = -> Binder125
  Suppressed = false
  Type = 0
FEATURE [PartDesign::Boolean] Boolean018
  BaseFeature = -> Pad026
  Group = -> [Compound056]
  Suppressed = false
  Type = 1
  UsePlacement = false
FEATURE [PartDesign::Body] Body114  label="basement_v2_spacer"
  Group = -> [Binder123,Pad026,Boolean018]
  Origin = -> Origin089
  Tip = -> Boolean018
FEATURE [PartDesign::FeatureBase] BaseFeature001
  BaseFeature = -> Body114
  Suppressed = false
FEATURE [PartDesign::Pocket] Pocket122
  BaseFeature = -> BaseFeature001
  Direction = (0,0,-1)
  Length = 7
  Length2 = 5
  Profile = -> Sketch200
  ReferenceAxis = -> Sketch200 [N_Axis]
  Reversed = true
  Suppressed = false
  Type = 0
FEATURE [PartDesign::Body] Body115  label="basement_v2_spacer2"
  BaseFeature = -> Body114
  Group = -> [BaseFeature001,Sketch199,Sketch200,Pocket122]
  Origin = -> Origin090
  Tip = -> Pocket122
  expr: BaseFeature = <<basement_v2_spacer>>._self
FEATURE [Sketcher::SketchObject] Sketch204
  AttachmentOffset = pos=(0,370,0) rot=(0,0,1;0rad)
  AttachmentSupport = -> [XY_Plane092]
  FullyConstrained = true
  MapMode = 5
  Placement = pos=(0,370,0) rot=(0,0,1;0rad)
  sketch-geometry (1):
    g0: Circle CenterX=0 CenterY=0 CenterZ=0 NormalX=0 NormalY=0 NormalZ=1 AngleXU=0 Radius=4
  constraints (2):
    c: Coincident(g0,g-1)
    c: Diameter(g0) = 8
FEATURE [PartDesign::Hole] Hole021
  BaseFeature = -> Pad028
  CustomThreadClearance = 0
  Depth = 25
  DepthType = 0
  Diameter = 8
  DrillForDepth = false
  DrillPoint = 1
  DrillPointAngle = 118
  HoleCutCountersinkAngle = 90
  HoleCutCustomValues = false
  HoleCutDepth = 0
  HoleCutDiameter = 6.1
  HoleCutType = 0
  ModelThread = false
  Profile = -> Sketch204
  Reversed = true
  Suppressed = false
  Tapered = false
  TaperedAngle = 90
  ThreadClass = 0
  ThreadDepth = 25
  ThreadDepthType = 0
  ThreadDirection = 0
  ThreadFit = 0
  ThreadSize = 0
  ThreadType = 0
  Threaded = false
  UseCustomThreadClearance = false
FEATURE [PartDesign::PolarPattern] PolarPattern011
  Angle = 360
  Axis = -> Z_Axis092
  BaseFeature = -> Hole021
  Mode = 0
  Occurrences = 3
  Offset = 120
  Originals = -> [Hole021]
  Suppressed = false
FEATURE [PartDesign::Boolean] Boolean019
  BaseFeature = -> PolarPattern011
  Group = -> [Compound059]
  Suppressed = false
  Type = 1
  UsePlacement = false
FEATURE [PartDesign::Body] Body117  label="basement_v2_bottom"
  Group = -> [Binder125,Pad028,Sketch204,Hole021,PolarPattern011,Boolean019]
  Origin = -> Origin092
  Tip = -> Boolean019
COMPONENT P78 — recipe-attached ("basement_v3", modeled in this document).
Construction recipe (the document's own serialized feature program — sketch geometry with constraints, then the solid features built on it; lengths are millimeters unless a unit is written):

FEATURE [PartDesign::SubShapeBinder] Binder126
  BindCopyOnChange = 0
  BindMode = 0
  ClaimChildren = true
  Context = -> Part021 [Body118.Binder126.]
  Fuse = false
  MakeFace = true
  OffsetFill = false
  OffsetIntersection = false
  OffsetJoinType = 0
  OffsetOpenResult = false
  PartialLoad = false
  Relative = false
  Support = -> [Array010]
  _Version = 2
FEATURE [PartDesign::FeaturePython] BaseBend047  # WARN: FeaturePython — macro-defined, semantics opaque (R4)
  BendSide = 0
  BendSketch = -> Binder126
  MidPlane = false
  Reverse = false
  Suppressed = false
  length = 100
  radius = 1
  thickness = 1
FEATURE [PartDesign::SubShapeBinder] Binder127
  BindCopyOnChange = 0
  BindMode = 0
  ClaimChildren = true
  Context = -> Part021 [Body119.Binder127.]
  Fuse = true
  MakeFace = true
  OffsetFill = false
  OffsetIntersection = false
  OffsetJoinType = 0
  OffsetOpenResult = false
  PartialLoad = false
  Relative = true
  Support = -> [Connect003]
  _Version = 2
FEATURE [PartDesign::FeaturePython] BaseBend048  # WARN: FeaturePython — macro-defined, semantics opaque (R4)
  BendSide = 0
  BendSketch = -> Binder127
  MidPlane = false
  Reverse = false
  Suppressed = false
  length = 100
  radius = 1
  thickness = 3
FEATURE [Sketcher::SketchObject] Sketch213
  AttachmentOffset = pos=(0,0,3) rot=(0,0,1;0rad)
  AttachmentSupport = -> [XY_Plane095]
  FullyConstrained = false
  MapMode = 5
  Placement = pos=(0,0,3) rot=(0,0,1;0rad)
  sketch-geometry (4):
    g0: LineSegment StartX=-416.278 StartY=-313.21 StartZ=0 EndX=489.891 EndY=-313.21 EndZ=0
    g1: LineSegment StartX=489.891 StartY=-313.21 StartZ=0 EndX=489.891 EndY=399.547 EndZ=0
    g2: LineSegment StartX=489.891 StartY=399.547 StartZ=0 EndX=-416.278 EndY=399.547 EndZ=0
    g3: LineSegment StartX=-416.278 StartY=399.547 StartZ=0 EndX=-416.278 EndY=-313.21 EndZ=0
  constraints (8):
    c: Coincident(g0,g1)
    c: Coincident(g1,g2)
    c: Coincident(g2,g3)
    c: Coincident(g3,g0)
    c: Horizontal(g0)
    c: Horizontal(g2)
    c: Vertical(g1)
    c: Vertical(g3)
FEATURE [PartDesign::Pad] Pad031
  BaseFeature = -> BaseBend048
  Direction = (0,0,1)
  Length = 10
  Length2 = 10
  Profile = -> Binder127
  Refine = true
  Suppressed = false
  Type = 0
FEATURE [PartDesign::Pocket] Pocket126
  BaseFeature = -> Pad031
  Direction = (0,0,-1)
  Length = 5
  Length2 = 5
  Profile = -> Sketch213
  ReferenceAxis = -> Sketch213 [N_Axis]
  Refine = true
  Reversed = true
  Suppressed = false
  Type = 1
FEATURE [PartDesign::FeaturePython] Bend028  # WARN: FeaturePython — macro-defined, semantics opaque (R4)
  AutoMiter = true
  BaseFeature = -> Pocket126
  BendType = 0
  LengthList = [10]
  LengthSpec = 0
  ReliefFactor = 0.7
  Suppressed = false
  UseReliefFactor = false
  angle = 90
  baseObject = -> Pocket126 [Edge4]
  bendAList = [90]
  extend1 = 0
  extend2 = 0
  gap1 = 0
  gap2 = 0
  invert = false
  kfactor = 0.5
  length = 10
  maxExtendDist = 5
  minGap = 0.1
  minReliefGap = 1
  miterangle1 = 0
  miterangle2 = 0
  offset = 0
  radius = 1
  reliefType = 0
  reliefd = 1
  reliefw = 0.8
  sketchflip = false
  sketchinvert = false
  unfold = false
  expr: baseObject = tuple(<<Pocket126>>._self; list(<<Edge4>>))
  expr: radius = BaseBend048.radius
FEATURE [PartDesign::FeatureAdditivePython] PDW_Add001  # link proxy (typed FeaturePython)
  BaseFeature = -> Bend028
  Body = Body119
  ClaimChildren = false
  EditPlacementAdjustments = false
  Enabled = 1
  LinkedObject = -> Bend028
  MeshTolerance = 0.1
  PatternBaseOffset = 0
  PatternBaseScale = 1
  PatternBaseScaleXYZ = (1,1,1)
  PatternOffsetCut = false
  PatternOffsetIntersection = false
  PatternOffsetJoin = 0
  PatternOffsetMode = 0
  PatternOffsetSelfIntersection = false
  PatternOperation = 4
  PatternOperationDefault = None
  PatternScaleCut = false
  PatternShapeOffset = 0
  PatternShapeScale = 1
  PatternShapeScaleXYZ = (1,1,1)
  PatternTool = -> Bend028
  PatternToolOffset = 0
  PatternToolScale = 1
  PatternToolScaleXYZ = (1,1,1)
  RefineMesh = true
  ShapeManagement = 1
  ShowMeshProps = false
  ShowOffsetProps = false
  ShowScaleProps = false
  ShowWarnings = true
  Suppressed = false
  TipBaseOffset = 0
  TipBaseScale = 1
  TipBaseScaleXYZ = (1,1,1)
  TipOffsetCut = false
  TipOffsetIntersection = false
  TipOffsetJoin = 0
  TipOffsetMode = 0
  TipOffsetSelfIntersection = false
  TipOperation = 0
  TipOperationDefault = Fuse
  TipScaleCut = false
  TipShapeOffset = 0
  TipShapeScale = 1
  TipShapeScaleXYZ = (1,1,1)
  TipTool = -> Bend028
  TipToolOffset = 0
  TipToolScale = 1
  TipToolScaleXYZ = (1,1,1)
  Type = Additive
  UsePatternBaseAddSubShape = false
  UsePatternToolAddSubShape = true
  UseTipBaseAddSubShape = false
  UseTipToolAddSubShape = true
  Version = 0.2023.08.13
FEATURE [PartDesign::PolarPattern] PolarPattern010
  Angle = 360
  Axis = -> Z_Axis095
  BaseFeature = -> PDW_Add001
  Mode = 0
  Occurrences = 3
  Offset = 120
  Originals = -> [PDW_Add001]
  Suppressed = false
FEATURE [Sketcher::SketchObject] Sketch214
  AttachmentOffset = pos=(0,0,1) rot=(0,0,1;0rad)
  AttachmentSupport = -> [XY_Plane094]
  FullyConstrained = false
  MapMode = 5
  Placement = pos=(0,0,1) rot=(0,0,1;0rad)
  expr: .AttachmentOffset.Base.z = <<BaseBend047>>.thickness
  sketch-geometry (4):
    g0: LineSegment StartX=-1342.32 StartY=-909.255 StartZ=0 EndX=1751.43 EndY=-909.255 EndZ=0
    g1: LineSegment StartX=1751.43 StartY=-909.255 StartZ=0 EndX=1751.43 EndY=1451 EndZ=0
    g2: LineSegment StartX=1751.43 StartY=1451 StartZ=0 EndX=-1342.32 EndY=1451 EndZ=0
    g3: LineSegment StartX=-1342.32 StartY=1451 StartZ=0 EndX=-1342.32 EndY=-909.255 EndZ=0
  constraints (8):
    c: Coincident(g0,g1)
    c: Coincident(g1,g2)
    c: Coincident(g2,g3)
    c: Coincident(g3,g0)
    c: Horizontal(g0)
    c: Horizontal(g2)
    c: Vertical(g1)
    c: Vertical(g3)
FEATURE [PartDesign::Pad] Pad032
  BaseFeature = -> BaseBend047
  Direction = (0,0,1)
  Length = 10
  Length2 = 10
  Profile = -> Sketch214
  ReferenceAxis = -> Sketch214 [N_Axis]
  Refine = true
  Suppressed = false
  Type = 0
FEATURE [PartDesign::Pocket] Pocket127
  BaseFeature = -> Pad032
  Direction = (0,0,-1)
  Length = 5
  Length2 = 5
  Profile = -> Sketch214
  ReferenceAxis = -> Sketch214 [N_Axis]
  Reversed = true
  Suppressed = false
  Type = 1
FEATURE [PartDesign::FeaturePython] Bend027  # WARN: FeaturePython — macro-defined, semantics opaque (R4)
  AutoMiter = true
  BaseFeature = -> Pocket127
  BendType = 0
  LengthList = [10]
  LengthSpec = 0
  ReliefFactor = 0.7
  Suppressed = false
  UseReliefFactor = false
  angle = 90
  baseObject = -> Pocket127 [Edge4]
  bendAList = [90]
  extend1 = 0
  extend2 = 0
  gap1 = 0
  gap2 = 0
  invert = false
  kfactor = 0.5
  length = 10
  maxExtendDist = 5
  minGap = 0.1
  minReliefGap = 1
  miterangle1 = 0
  miterangle2 = 0
  offset = 0
  radius = 1
  reliefType = 0
  reliefd = 1
  reliefw = 0.8
  sketchflip = false
  sketchinvert = false
  unfold = false
  expr: radius = BaseBend047.radius
FEATURE [PartDesign::FeatureAdditivePython] PDW_Common_Add003  # link proxy (typed FeaturePython)
  BaseFeature = -> Bend027
  Body = Body118
  ClaimChildren = false
  EditPlacementAdjustments = false
  Enabled = 1
  LinkedObject = -> Bend027
  MeshTolerance = 0.1
  PatternBase = -> BaseBend047
  PatternBaseOffset = 0
  PatternBaseScale = 1
  PatternBaseScaleXYZ = (1,1,1)
  PatternOffsetCut = false
  PatternOffsetIntersection = false
  PatternOffsetJoin = 0
  PatternOffsetMode = 0
  PatternOffsetSelfIntersection = false
  PatternOperation = 4
  PatternOperationDefault = Common
  PatternScaleCut = false
  PatternShapeOffset = 0
  PatternShapeScale = 1
  PatternShapeScaleXYZ = (1,1,1)
  PatternTool = -> Bend027
  PatternToolOffset = 0
  PatternToolScale = 1
  PatternToolScaleXYZ = (1,1,1)
  RefineMesh = true
  ShapeManagement = 1
  ShowMeshProps = false
  ShowOffsetProps = false
  ShowScaleProps = false
  ShowWarnings = true
  Suppressed = false
  TipBase = -> BaseBend047
  TipBaseOffset = 0
  TipBaseScale = 1
  TipBaseScaleXYZ = (1,1,1)
  TipOffsetCut = false
  TipOffsetIntersection = false
  TipOffsetJoin = 0
  TipOffsetMode = 0
  TipOffsetSelfIntersection = false
  TipOperation = 0
  TipOperationDefault = Common
  TipScaleCut = false
  TipShapeOffset = 0
  TipShapeScale = 1
  TipShapeScaleXYZ = (1,1,1)
  TipTool = -> Bend027
  TipToolOffset = 0
  TipToolScale = 1
  TipToolScaleXYZ = (1,1,1)
  Type = Additive
  UsePatternBaseAddSubShape = false
  UsePatternToolAddSubShape = true
  UseTipBaseAddSubShape = false
  UseTipToolAddSubShape = true
  Version = 0.2023.08.13
FEATURE [PartDesign::PolarPattern] PolarPattern009
  Angle = 360
  Axis = -> Z_Axis094
  BaseFeature = -> PDW_Common_Add003
  Mode = 0
  Occurrences = 3
  Offset = 120
  Originals = -> [PDW_Common_Add003]
  Suppressed = false
FEATURE [PartDesign::Boolean] Boolean025
  BaseFeature = -> PolarPattern009
  Group = -> [Compound068]
  Suppressed = false
  Type = 1
  UsePlacement = false
FEATURE [PartDesign::Body] Body118  label="basement_v3_bottom_material_0.50ansi"
  Group = -> [Binder126,BaseBend047,Sketch214,Pad032,Pocket127,Bend027,PDW_Common_Add003,PolarPattern009,Boolean025]
  Origin = -> Origin094
  Placement = pos=(0,0,-70) rot=(0,0,1;0rad)
  Tip = -> Pocket127
FEATURE [PartDesign::Boolean] Boolean024
  BaseFeature = -> PolarPattern010
  Group = -> [Compound067]
  Suppressed = false
  Type = 1
  UsePlacement = false
FEATURE [PartDesign::Body] Body119  label="basement_v3_top_material_0.50ansi"
  Group = -> [Binder127,Sketch213,BaseBend048,Pad031,Pocket126,Bend028,PDW_Add001,PolarPattern010,Boolean024]
  Origin = -> Origin095
  Tip = -> Pocket126
PROVENANCE & LICENSES
A FreeCAD (.FCStd) document from a public repository crawl; recipes are the document's own serialized feature recipes (and, for linked parts, companion documents' recipes).
License: as declared in the source repository (recorded in the dataset sidecar).
